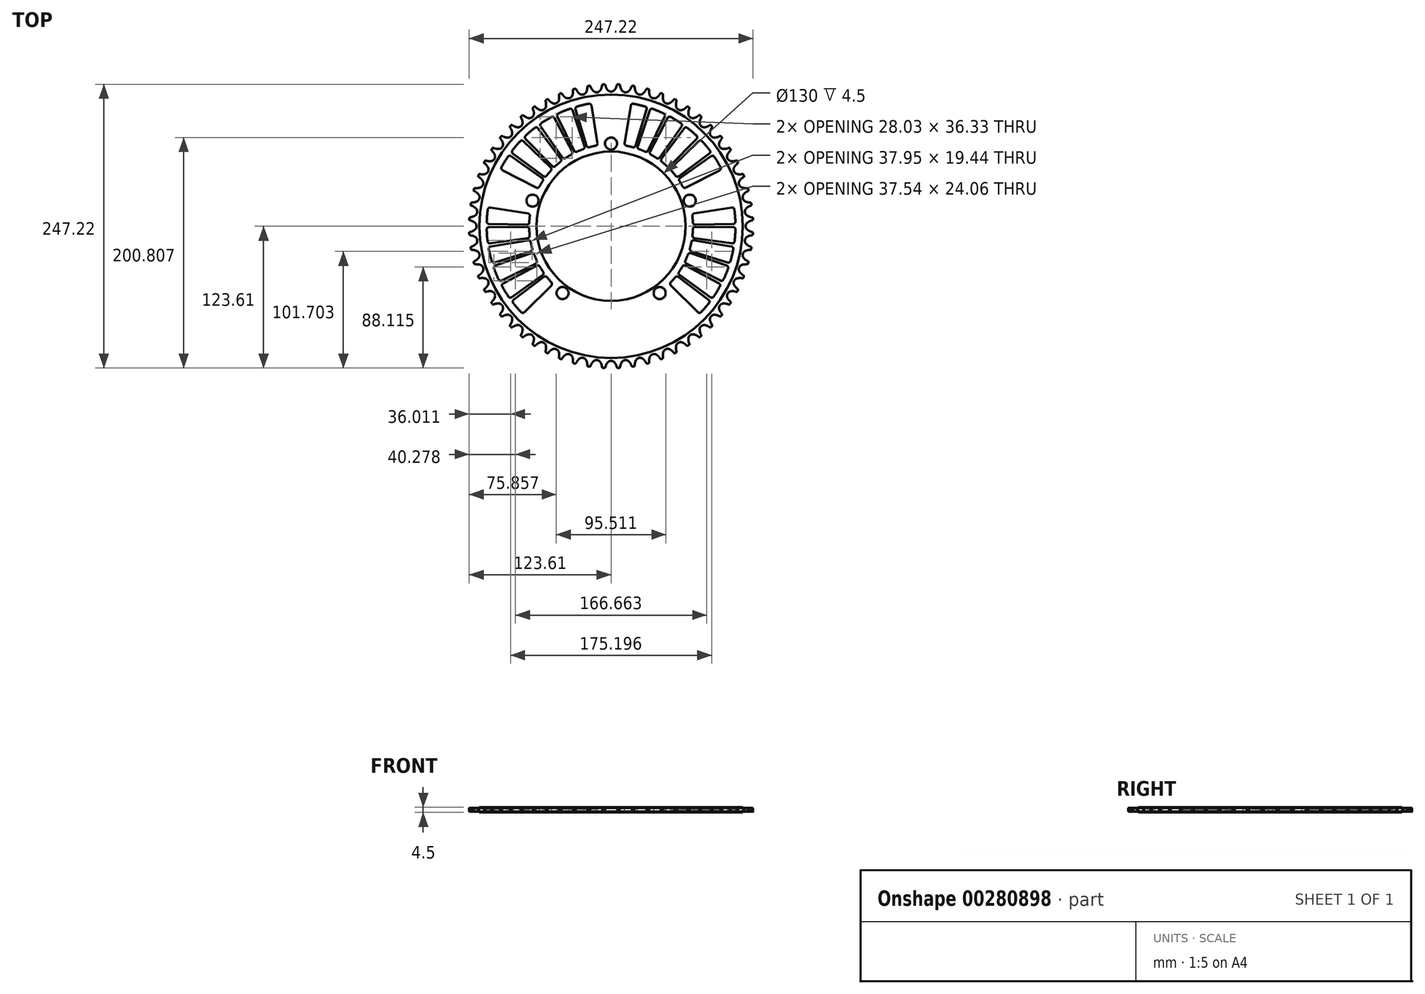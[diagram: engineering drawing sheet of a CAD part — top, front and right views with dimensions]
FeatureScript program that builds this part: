
annotation { "Feature Type Name" : "Feature", "Feature Type Description" : "" }
export const myFeature = defineFeature(function(context is Context, id is Id, definition is map)
    precondition{}
    {
        {
            var Q0;
            Q0=qCreatedBy(makeId("Top.planeOp"),FACE);
            var sketch = newSketch(context, id + "F0", { "sketchPlane" : qUnion([Q0])});
            skCircle(sketch, "E0", {"center": v(0, 0) * mm, "radius": 121.28 * mm, "construction": true});
            skArc(sketch, "E1", {"start": v(-3.25, 118.92) * mm, "mid": v(-1.82, 117.7) * mm, "end": v(0, 117.26) * mm});
            skArc(sketch, "E2", {"start": v(-4.69, 121.64) * mm, "mid": v(-4.07, 120.23) * mm, "end": v(-3.25, 118.92) * mm});
            skLineSegment(sketch, "E3", {"start": v(-4.69, 121.64) * mm, "end": v(-5.07, 122.77) * mm});
            skArc(sketch, "E4.trimOffspring", {"start": v(-5.07, 122.77) * mm, "mid": v(-5.68, 124.05) * mm, "end": v(-6.56, 125.17) * mm});
            skArc(sketch, "E5.MirrorCS", {"start": v(3.25, 118.92) * mm, "mid": v(1.82, 117.7) * mm, "end": v(0, 117.26) * mm});
            skArc(sketch, "E6.MirrorCS", {"start": v(4.69, 121.64) * mm, "mid": v(4.07, 120.23) * mm, "end": v(3.25, 118.92) * mm});
            skLineSegment(sketch, "E7.MirrorCS", {"start": v(4.69, 121.64) * mm, "end": v(5.07, 122.77) * mm});
            skArc(sketch, "E8.MirrorCS", {"start": v(5.07, 122.77) * mm, "mid": v(5.68, 124.05) * mm, "end": v(6.56, 125.17) * mm});
            skArc(sketch, "E9.1.1", {"start": v(-17.37, 120.49) * mm, "mid": v(-16.61, 119.14) * mm, "end": v(-15.66, 117.93) * mm});
            skArc(sketch, "E9.1.2", {"start": v(-8.06, 121.47) * mm, "mid": v(-8.52, 120) * mm, "end": v(-9.2, 118.6) * mm});
            skArc(sketch, "E9.1.3", {"start": v(-9.2, 118.6) * mm, "mid": v(-10.49, 117.24) * mm, "end": v(-12.26, 116.62) * mm});
            skArc(sketch, "E9.1.4", {"start": v(-7.79, 122.62) * mm, "mid": v(-7.32, 123.97) * mm, "end": v(-6.56, 125.17) * mm});
            skArc(sketch, "E9.1.5", {"start": v(-17.88, 121.56) * mm, "mid": v(-18.62, 122.78) * mm, "end": v(-19.6, 123.8) * mm});
            skArc(sketch, "E9.1.6", {"start": v(-15.66, 117.93) * mm, "mid": v(-14.12, 116.86) * mm, "end": v(-12.26, 116.62) * mm});
            skLineSegment(sketch, "E9.1.7", {"start": v(-17.37, 120.49) * mm, "end": v(-17.88, 121.56) * mm});
            skLineSegment(sketch, "E9.1.8", {"start": v(-8.06, 121.47) * mm, "end": v(-7.79, 122.62) * mm});
            skArc(sketch, "E9.2.1", {"start": v(-29.87, 118) * mm, "mid": v(-28.98, 116.75) * mm, "end": v(-27.9, 115.64) * mm});
            skArc(sketch, "E9.2.2", {"start": v(-20.7, 119.96) * mm, "mid": v(-21.02, 118.44) * mm, "end": v(-21.55, 117) * mm});
            skArc(sketch, "E9.2.3", {"start": v(-21.55, 117) * mm, "mid": v(-22.69, 115.5) * mm, "end": v(-24.38, 114.7) * mm});
            skArc(sketch, "E9.2.4", {"start": v(-20.56, 121.14) * mm, "mid": v(-20.24, 122.52) * mm, "end": v(-19.6, 123.8) * mm});
            skArc(sketch, "E9.2.5", {"start": v(-30.49, 119.03) * mm, "mid": v(-31.35, 120.16) * mm, "end": v(-32.44, 121.08) * mm});
            skArc(sketch, "E9.2.6", {"start": v(-27.9, 115.64) * mm, "mid": v(-26.25, 114.75) * mm, "end": v(-24.38, 114.7) * mm});
            skLineSegment(sketch, "E9.2.7", {"start": v(-29.87, 118) * mm, "end": v(-30.49, 119.03) * mm});
            skLineSegment(sketch, "E9.2.8", {"start": v(-20.7, 119.96) * mm, "end": v(-20.56, 121.14) * mm});
            skArc(sketch, "E9.3.1", {"start": v(-42.05, 114.24) * mm, "mid": v(-41.02, 113.08) * mm, "end": v(-39.84, 112.1) * mm});
            skArc(sketch, "E9.3.2", {"start": v(-33.13, 117.14) * mm, "mid": v(-33.28, 115.6) * mm, "end": v(-33.66, 114.1) * mm});
            skArc(sketch, "E9.3.3", {"start": v(-33.66, 114.1) * mm, "mid": v(-34.64, 112.5) * mm, "end": v(-36.24, 111.52) * mm});
            skArc(sketch, "E9.3.4", {"start": v(-33.11, 118.33) * mm, "mid": v(-32.93, 119.74) * mm, "end": v(-32.44, 121.08) * mm});
            skArc(sketch, "E9.3.5", {"start": v(-42.76, 115.2) * mm, "mid": v(-43.74, 116.23) * mm, "end": v(-44.92, 117.02) * mm});
            skArc(sketch, "E9.3.6", {"start": v(-39.84, 112.1) * mm, "mid": v(-38.1, 111.37) * mm, "end": v(-36.24, 111.52) * mm});
            skLineSegment(sketch, "E9.3.7", {"start": v(-42.05, 114.24) * mm, "end": v(-42.76, 115.2) * mm});
            skLineSegment(sketch, "E9.3.8", {"start": v(-33.13, 117.14) * mm, "end": v(-33.11, 118.33) * mm});
            skArc(sketch, "E9.4.1", {"start": v(-53.76, 109.22) * mm, "mid": v(-52.62, 108.18) * mm, "end": v(-51.34, 107.31) * mm});
            skArc(sketch, "E9.4.2", {"start": v(-45.2, 113.03) * mm, "mid": v(-45.18, 111.49) * mm, "end": v(-45.4, 109.96) * mm});
            skArc(sketch, "E9.4.3", {"start": v(-45.4, 109.96) * mm, "mid": v(-46.2, 108.26) * mm, "end": v(-47.7, 107.12) * mm});
            skArc(sketch, "E9.4.4", {"start": v(-45.3, 114.22) * mm, "mid": v(-45.27, 115.64) * mm, "end": v(-44.92, 117.02) * mm});
            skArc(sketch, "E9.4.5", {"start": v(-54.57, 110.1) * mm, "mid": v(-55.65, 111.02) * mm, "end": v(-56.9, 111.68) * mm});
            skArc(sketch, "E9.4.6", {"start": v(-51.34, 107.31) * mm, "mid": v(-49.54, 106.78) * mm, "end": v(-47.7, 107.12) * mm});
            skLineSegment(sketch, "E9.4.7", {"start": v(-53.76, 109.22) * mm, "end": v(-54.57, 110.1) * mm});
            skLineSegment(sketch, "E9.4.8", {"start": v(-45.2, 113.03) * mm, "end": v(-45.3, 114.22) * mm});
            skArc(sketch, "E9.5.1", {"start": v(-64.88, 103) * mm, "mid": v(-63.64, 102.08) * mm, "end": v(-62.27, 101.36) * mm});
            skArc(sketch, "E9.5.2", {"start": v(-56.76, 107.69) * mm, "mid": v(-56.59, 106.15) * mm, "end": v(-56.64, 104.6) * mm});
            skArc(sketch, "E9.5.3", {"start": v(-56.64, 104.6) * mm, "mid": v(-57.27, 102.84) * mm, "end": v(-58.63, 101.55) * mm});
            skArc(sketch, "E9.5.4", {"start": v(-57, 108.85) * mm, "mid": v(-57.1, 110.27) * mm, "end": v(-56.9, 111.68) * mm});
            skArc(sketch, "E9.5.5", {"start": v(-65.78, 103.78) * mm, "mid": v(-66.95, 104.6) * mm, "end": v(-68.27, 105.12) * mm});
            skArc(sketch, "E9.5.6", {"start": v(-62.27, 101.36) * mm, "mid": v(-60.43, 101.02) * mm, "end": v(-58.63, 101.55) * mm});
            skLineSegment(sketch, "E9.5.7", {"start": v(-64.88, 103) * mm, "end": v(-65.78, 103.78) * mm});
            skLineSegment(sketch, "E9.5.8", {"start": v(-56.76, 107.69) * mm, "end": v(-57, 108.85) * mm});
            skArc(sketch, "E9.6.1", {"start": v(-75.3, 95.66) * mm, "mid": v(-73.96, 94.87) * mm, "end": v(-72.53, 94.3) * mm});
            skArc(sketch, "E9.6.2", {"start": v(-67.7, 101.16) * mm, "mid": v(-67.38, 99.66) * mm, "end": v(-67.27, 98.11) * mm});
            skArc(sketch, "E9.6.3", {"start": v(-67.27, 98.11) * mm, "mid": v(-67.7, 96.3) * mm, "end": v(-68.92, 94.87) * mm});
            skArc(sketch, "E9.6.4", {"start": v(-68.06, 102.3) * mm, "mid": v(-68.32, 103.7) * mm, "end": v(-68.27, 105.12) * mm});
            skArc(sketch, "E9.6.5", {"start": v(-76.26, 96.34) * mm, "mid": v(-77.51, 97.02) * mm, "end": v(-78.88, 97.41) * mm});
            skArc(sketch, "E9.6.6", {"start": v(-72.53, 94.3) * mm, "mid": v(-70.66, 94.15) * mm, "end": v(-68.92, 94.87) * mm});
            skLineSegment(sketch, "E9.6.7", {"start": v(-75.3, 95.66) * mm, "end": v(-76.26, 96.34) * mm});
            skLineSegment(sketch, "E9.6.8", {"start": v(-67.7, 101.16) * mm, "end": v(-68.06, 102.3) * mm});
            skArc(sketch, "E9.7.1", {"start": v(-84.88, 87.26) * mm, "mid": v(-83.47, 86.62) * mm, "end": v(-81.98, 86.2) * mm});
            skArc(sketch, "E9.7.2", {"start": v(-77.91, 93.53) * mm, "mid": v(-77.42, 92.07) * mm, "end": v(-77.16, 90.55) * mm});
            skArc(sketch, "E9.7.3", {"start": v(-77.16, 90.55) * mm, "mid": v(-77.4, 88.69) * mm, "end": v(-78.46, 87.14) * mm});
            skArc(sketch, "E9.7.4", {"start": v(-78.38, 94.63) * mm, "mid": v(-78.79, 96) * mm, "end": v(-78.88, 97.41) * mm});
            skArc(sketch, "E9.7.5", {"start": v(-85.92, 87.84) * mm, "mid": v(-87.23, 88.39) * mm, "end": v(-88.63, 88.63) * mm});
            skArc(sketch, "E9.7.6", {"start": v(-81.98, 86.2) * mm, "mid": v(-80.11, 86.25) * mm, "end": v(-78.46, 87.14) * mm});
            skLineSegment(sketch, "E9.7.7", {"start": v(-84.88, 87.26) * mm, "end": v(-85.92, 87.84) * mm});
            skLineSegment(sketch, "E9.7.8", {"start": v(-77.91, 93.53) * mm, "end": v(-78.38, 94.63) * mm});
            skArc(sketch, "E9.8.1", {"start": v(-93.53, 77.91) * mm, "mid": v(-92.07, 77.42) * mm, "end": v(-90.55, 77.16) * mm});
            skArc(sketch, "E9.8.2", {"start": v(-87.26, 84.88) * mm, "mid": v(-86.62, 83.47) * mm, "end": v(-86.2, 81.98) * mm});
            skArc(sketch, "E9.8.3", {"start": v(-86.2, 81.98) * mm, "mid": v(-86.25, 80.11) * mm, "end": v(-87.14, 78.46) * mm});
            skArc(sketch, "E9.8.4", {"start": v(-87.84, 85.92) * mm, "mid": v(-88.39, 87.23) * mm, "end": v(-88.63, 88.63) * mm});
            skArc(sketch, "E9.8.5", {"start": v(-94.63, 78.38) * mm, "mid": v(-96, 78.79) * mm, "end": v(-97.41, 78.88) * mm});
            skArc(sketch, "E9.8.6", {"start": v(-90.55, 77.16) * mm, "mid": v(-88.69, 77.4) * mm, "end": v(-87.14, 78.46) * mm});
            skLineSegment(sketch, "E9.8.7", {"start": v(-93.53, 77.91) * mm, "end": v(-94.63, 78.38) * mm});
            skLineSegment(sketch, "E9.8.8", {"start": v(-87.26, 84.88) * mm, "end": v(-87.84, 85.92) * mm});
            skArc(sketch, "E9.9.1", {"start": v(-101.16, 67.7) * mm, "mid": v(-99.66, 67.38) * mm, "end": v(-98.11, 67.27) * mm});
            skArc(sketch, "E9.9.2", {"start": v(-95.66, 75.3) * mm, "mid": v(-94.87, 73.96) * mm, "end": v(-94.3, 72.53) * mm});
            skArc(sketch, "E9.9.3", {"start": v(-94.3, 72.53) * mm, "mid": v(-94.15, 70.66) * mm, "end": v(-94.87, 68.92) * mm});
            skArc(sketch, "E9.9.4", {"start": v(-96.34, 76.26) * mm, "mid": v(-97.02, 77.51) * mm, "end": v(-97.41, 78.88) * mm});
            skArc(sketch, "E9.9.5", {"start": v(-102.3, 68.06) * mm, "mid": v(-103.7, 68.32) * mm, "end": v(-105.12, 68.27) * mm});
            skArc(sketch, "E9.9.6", {"start": v(-98.11, 67.27) * mm, "mid": v(-96.3, 67.7) * mm, "end": v(-94.87, 68.92) * mm});
            skLineSegment(sketch, "E9.9.7", {"start": v(-101.16, 67.7) * mm, "end": v(-102.3, 68.06) * mm});
            skLineSegment(sketch, "E9.9.8", {"start": v(-95.66, 75.3) * mm, "end": v(-96.34, 76.26) * mm});
            skArc(sketch, "E9.10.1", {"start": v(-107.69, 56.76) * mm, "mid": v(-106.15, 56.59) * mm, "end": v(-104.6, 56.64) * mm});
            skArc(sketch, "E9.10.2", {"start": v(-103, 64.88) * mm, "mid": v(-102.08, 63.64) * mm, "end": v(-101.36, 62.27) * mm});
            skArc(sketch, "E9.10.3", {"start": v(-101.36, 62.27) * mm, "mid": v(-101.02, 60.43) * mm, "end": v(-101.55, 58.63) * mm});
            skArc(sketch, "E9.10.4", {"start": v(-103.78, 65.78) * mm, "mid": v(-104.6, 66.95) * mm, "end": v(-105.12, 68.27) * mm});
            skArc(sketch, "E9.10.5", {"start": v(-108.85, 57) * mm, "mid": v(-110.27, 57.1) * mm, "end": v(-111.68, 56.9) * mm});
            skArc(sketch, "E9.10.6", {"start": v(-104.6, 56.64) * mm, "mid": v(-102.84, 57.27) * mm, "end": v(-101.55, 58.63) * mm});
            skLineSegment(sketch, "E9.10.7", {"start": v(-107.69, 56.76) * mm, "end": v(-108.85, 57) * mm});
            skLineSegment(sketch, "E9.10.8", {"start": v(-103, 64.88) * mm, "end": v(-103.78, 65.78) * mm});
            skArc(sketch, "E9.11.1", {"start": v(-113.03, 45.2) * mm, "mid": v(-111.49, 45.18) * mm, "end": v(-109.96, 45.4) * mm});
            skArc(sketch, "E9.11.2", {"start": v(-109.22, 53.76) * mm, "mid": v(-108.18, 52.62) * mm, "end": v(-107.31, 51.34) * mm});
            skArc(sketch, "E9.11.3", {"start": v(-107.31, 51.34) * mm, "mid": v(-106.78, 49.54) * mm, "end": v(-107.12, 47.7) * mm});
            skArc(sketch, "E9.11.4", {"start": v(-110.1, 54.57) * mm, "mid": v(-111.02, 55.65) * mm, "end": v(-111.68, 56.9) * mm});
            skArc(sketch, "E9.11.5", {"start": v(-114.22, 45.3) * mm, "mid": v(-115.64, 45.27) * mm, "end": v(-117.02, 44.92) * mm});
            skArc(sketch, "E9.11.6", {"start": v(-109.96, 45.4) * mm, "mid": v(-108.26, 46.2) * mm, "end": v(-107.12, 47.7) * mm});
            skLineSegment(sketch, "E9.11.7", {"start": v(-113.03, 45.2) * mm, "end": v(-114.22, 45.3) * mm});
            skLineSegment(sketch, "E9.11.8", {"start": v(-109.22, 53.76) * mm, "end": v(-110.1, 54.57) * mm});
            skArc(sketch, "E9.12.1", {"start": v(-117.14, 33.13) * mm, "mid": v(-115.6, 33.28) * mm, "end": v(-114.1, 33.66) * mm});
            skArc(sketch, "E9.12.2", {"start": v(-114.24, 42.05) * mm, "mid": v(-113.08, 41.02) * mm, "end": v(-112.1, 39.84) * mm});
            skArc(sketch, "E9.12.3", {"start": v(-112.1, 39.84) * mm, "mid": v(-111.37, 38.1) * mm, "end": v(-111.52, 36.24) * mm});
            skArc(sketch, "E9.12.4", {"start": v(-115.2, 42.76) * mm, "mid": v(-116.23, 43.74) * mm, "end": v(-117.02, 44.92) * mm});
            skArc(sketch, "E9.12.5", {"start": v(-118.33, 33.11) * mm, "mid": v(-119.74, 32.93) * mm, "end": v(-121.08, 32.44) * mm});
            skArc(sketch, "E9.12.6", {"start": v(-114.1, 33.66) * mm, "mid": v(-112.5, 34.64) * mm, "end": v(-111.52, 36.24) * mm});
            skLineSegment(sketch, "E9.12.7", {"start": v(-117.14, 33.13) * mm, "end": v(-118.33, 33.11) * mm});
            skLineSegment(sketch, "E9.12.8", {"start": v(-114.24, 42.05) * mm, "end": v(-115.2, 42.76) * mm});
            skArc(sketch, "E9.13.1", {"start": v(-119.96, 20.7) * mm, "mid": v(-118.44, 21.02) * mm, "end": v(-117, 21.55) * mm});
            skArc(sketch, "E9.13.2", {"start": v(-118, 29.87) * mm, "mid": v(-116.75, 28.98) * mm, "end": v(-115.64, 27.9) * mm});
            skArc(sketch, "E9.13.3", {"start": v(-115.64, 27.9) * mm, "mid": v(-114.75, 26.25) * mm, "end": v(-114.7, 24.38) * mm});
            skArc(sketch, "E9.13.4", {"start": v(-119.03, 30.49) * mm, "mid": v(-120.16, 31.35) * mm, "end": v(-121.08, 32.44) * mm});
            skArc(sketch, "E9.13.5", {"start": v(-121.14, 20.56) * mm, "mid": v(-122.52, 20.24) * mm, "end": v(-123.8, 19.6) * mm});
            skArc(sketch, "E9.13.6", {"start": v(-117, 21.55) * mm, "mid": v(-115.5, 22.69) * mm, "end": v(-114.7, 24.38) * mm});
            skLineSegment(sketch, "E9.13.7", {"start": v(-119.96, 20.7) * mm, "end": v(-121.14, 20.56) * mm});
            skLineSegment(sketch, "E9.13.8", {"start": v(-118, 29.87) * mm, "end": v(-119.03, 30.49) * mm});
            skArc(sketch, "E9.14.1", {"start": v(-121.47, 8.06) * mm, "mid": v(-120, 8.52) * mm, "end": v(-118.6, 9.2) * mm});
            skArc(sketch, "E9.14.2", {"start": v(-120.49, 17.37) * mm, "mid": v(-119.14, 16.61) * mm, "end": v(-117.93, 15.66) * mm});
            skArc(sketch, "E9.14.3", {"start": v(-117.93, 15.66) * mm, "mid": v(-116.86, 14.12) * mm, "end": v(-116.62, 12.26) * mm});
            skArc(sketch, "E9.14.4", {"start": v(-121.56, 17.88) * mm, "mid": v(-122.78, 18.62) * mm, "end": v(-123.8, 19.6) * mm});
            skArc(sketch, "E9.14.5", {"start": v(-122.62, 7.79) * mm, "mid": v(-123.97, 7.32) * mm, "end": v(-125.17, 6.56) * mm});
            skArc(sketch, "E9.14.6", {"start": v(-118.6, 9.2) * mm, "mid": v(-117.24, 10.49) * mm, "end": v(-116.62, 12.26) * mm});
            skLineSegment(sketch, "E9.14.7", {"start": v(-121.47, 8.06) * mm, "end": v(-122.62, 7.79) * mm});
            skLineSegment(sketch, "E9.14.8", {"start": v(-120.49, 17.37) * mm, "end": v(-121.56, 17.88) * mm});
            skArc(sketch, "E9.15.1", {"start": v(-121.64, -4.69) * mm, "mid": v(-120.23, -4.07) * mm, "end": v(-118.92, -3.25) * mm});
            skArc(sketch, "E9.15.2", {"start": v(-121.64, 4.69) * mm, "mid": v(-120.23, 4.07) * mm, "end": v(-118.92, 3.25) * mm});
            skArc(sketch, "E9.15.3", {"start": v(-118.92, 3.25) * mm, "mid": v(-117.7, 1.82) * mm, "end": v(-117.26, 0) * mm});
            skArc(sketch, "E9.15.4", {"start": v(-122.77, 5.07) * mm, "mid": v(-124.05, 5.68) * mm, "end": v(-125.17, 6.56) * mm});
            skArc(sketch, "E9.15.5", {"start": v(-122.77, -5.07) * mm, "mid": v(-124.05, -5.68) * mm, "end": v(-125.17, -6.56) * mm});
            skArc(sketch, "E9.15.6", {"start": v(-118.92, -3.25) * mm, "mid": v(-117.7, -1.82) * mm, "end": v(-117.26, 0) * mm});
            skLineSegment(sketch, "E9.15.7", {"start": v(-121.64, -4.69) * mm, "end": v(-122.77, -5.07) * mm});
            skLineSegment(sketch, "E9.15.8", {"start": v(-121.64, 4.69) * mm, "end": v(-122.77, 5.07) * mm});
            skArc(sketch, "E9.16.1", {"start": v(-120.49, -17.37) * mm, "mid": v(-119.14, -16.61) * mm, "end": v(-117.93, -15.66) * mm});
            skArc(sketch, "E9.16.2", {"start": v(-121.47, -8.06) * mm, "mid": v(-120, -8.52) * mm, "end": v(-118.6, -9.2) * mm});
            skArc(sketch, "E9.16.3", {"start": v(-118.6, -9.2) * mm, "mid": v(-117.24, -10.49) * mm, "end": v(-116.62, -12.26) * mm});
            skArc(sketch, "E9.16.4", {"start": v(-122.62, -7.79) * mm, "mid": v(-123.97, -7.32) * mm, "end": v(-125.17, -6.56) * mm});
            skArc(sketch, "E9.16.5", {"start": v(-121.56, -17.88) * mm, "mid": v(-122.78, -18.62) * mm, "end": v(-123.8, -19.6) * mm});
            skArc(sketch, "E9.16.6", {"start": v(-117.93, -15.66) * mm, "mid": v(-116.86, -14.12) * mm, "end": v(-116.62, -12.26) * mm});
            skLineSegment(sketch, "E9.16.7", {"start": v(-120.49, -17.37) * mm, "end": v(-121.56, -17.88) * mm});
            skLineSegment(sketch, "E9.16.8", {"start": v(-121.47, -8.06) * mm, "end": v(-122.62, -7.79) * mm});
            skArc(sketch, "E9.17.1", {"start": v(-118, -29.87) * mm, "mid": v(-116.75, -28.98) * mm, "end": v(-115.64, -27.9) * mm});
            skArc(sketch, "E9.17.2", {"start": v(-119.96, -20.7) * mm, "mid": v(-118.44, -21.02) * mm, "end": v(-117, -21.55) * mm});
            skArc(sketch, "E9.17.3", {"start": v(-117, -21.55) * mm, "mid": v(-115.5, -22.69) * mm, "end": v(-114.7, -24.38) * mm});
            skArc(sketch, "E9.17.4", {"start": v(-121.14, -20.56) * mm, "mid": v(-122.52, -20.24) * mm, "end": v(-123.8, -19.6) * mm});
            skArc(sketch, "E9.17.5", {"start": v(-119.03, -30.49) * mm, "mid": v(-120.16, -31.35) * mm, "end": v(-121.08, -32.44) * mm});
            skArc(sketch, "E9.17.6", {"start": v(-115.64, -27.9) * mm, "mid": v(-114.75, -26.25) * mm, "end": v(-114.7, -24.38) * mm});
            skLineSegment(sketch, "E9.17.7", {"start": v(-118, -29.87) * mm, "end": v(-119.03, -30.49) * mm});
            skLineSegment(sketch, "E9.17.8", {"start": v(-119.96, -20.7) * mm, "end": v(-121.14, -20.56) * mm});
            skArc(sketch, "E9.18.1", {"start": v(-114.24, -42.05) * mm, "mid": v(-113.08, -41.02) * mm, "end": v(-112.1, -39.84) * mm});
            skArc(sketch, "E9.18.2", {"start": v(-117.14, -33.13) * mm, "mid": v(-115.6, -33.28) * mm, "end": v(-114.1, -33.66) * mm});
            skArc(sketch, "E9.18.3", {"start": v(-114.1, -33.66) * mm, "mid": v(-112.5, -34.64) * mm, "end": v(-111.52, -36.24) * mm});
            skArc(sketch, "E9.18.4", {"start": v(-118.33, -33.11) * mm, "mid": v(-119.74, -32.93) * mm, "end": v(-121.08, -32.44) * mm});
            skArc(sketch, "E9.18.5", {"start": v(-115.2, -42.76) * mm, "mid": v(-116.23, -43.74) * mm, "end": v(-117.02, -44.92) * mm});
            skArc(sketch, "E9.18.6", {"start": v(-112.1, -39.84) * mm, "mid": v(-111.37, -38.1) * mm, "end": v(-111.52, -36.24) * mm});
            skLineSegment(sketch, "E9.18.7", {"start": v(-114.24, -42.05) * mm, "end": v(-115.2, -42.76) * mm});
            skLineSegment(sketch, "E9.18.8", {"start": v(-117.14, -33.13) * mm, "end": v(-118.33, -33.11) * mm});
            skArc(sketch, "E9.19.1", {"start": v(-109.22, -53.76) * mm, "mid": v(-108.18, -52.62) * mm, "end": v(-107.31, -51.34) * mm});
            skArc(sketch, "E9.19.2", {"start": v(-113.03, -45.2) * mm, "mid": v(-111.49, -45.18) * mm, "end": v(-109.96, -45.4) * mm});
            skArc(sketch, "E9.19.3", {"start": v(-109.96, -45.4) * mm, "mid": v(-108.26, -46.2) * mm, "end": v(-107.12, -47.7) * mm});
            skArc(sketch, "E9.19.4", {"start": v(-114.22, -45.3) * mm, "mid": v(-115.64, -45.27) * mm, "end": v(-117.02, -44.92) * mm});
            skArc(sketch, "E9.19.5", {"start": v(-110.1, -54.57) * mm, "mid": v(-111.02, -55.65) * mm, "end": v(-111.68, -56.9) * mm});
            skArc(sketch, "E9.19.6", {"start": v(-107.31, -51.34) * mm, "mid": v(-106.78, -49.54) * mm, "end": v(-107.12, -47.7) * mm});
            skLineSegment(sketch, "E9.19.7", {"start": v(-109.22, -53.76) * mm, "end": v(-110.1, -54.57) * mm});
            skLineSegment(sketch, "E9.19.8", {"start": v(-113.03, -45.2) * mm, "end": v(-114.22, -45.3) * mm});
            skArc(sketch, "E9.20.1", {"start": v(-103, -64.88) * mm, "mid": v(-102.08, -63.64) * mm, "end": v(-101.36, -62.27) * mm});
            skArc(sketch, "E9.20.2", {"start": v(-107.69, -56.76) * mm, "mid": v(-106.15, -56.59) * mm, "end": v(-104.6, -56.64) * mm});
            skArc(sketch, "E9.20.3", {"start": v(-104.6, -56.64) * mm, "mid": v(-102.84, -57.27) * mm, "end": v(-101.55, -58.63) * mm});
            skArc(sketch, "E9.20.4", {"start": v(-108.85, -57) * mm, "mid": v(-110.27, -57.1) * mm, "end": v(-111.68, -56.9) * mm});
            skArc(sketch, "E9.20.5", {"start": v(-103.78, -65.78) * mm, "mid": v(-104.6, -66.95) * mm, "end": v(-105.12, -68.27) * mm});
            skArc(sketch, "E9.20.6", {"start": v(-101.36, -62.27) * mm, "mid": v(-101.02, -60.43) * mm, "end": v(-101.55, -58.63) * mm});
            skLineSegment(sketch, "E9.20.7", {"start": v(-103, -64.88) * mm, "end": v(-103.78, -65.78) * mm});
            skLineSegment(sketch, "E9.20.8", {"start": v(-107.69, -56.76) * mm, "end": v(-108.85, -57) * mm});
            skArc(sketch, "E9.21.1", {"start": v(-95.66, -75.3) * mm, "mid": v(-94.87, -73.96) * mm, "end": v(-94.3, -72.53) * mm});
            skArc(sketch, "E9.21.2", {"start": v(-101.16, -67.7) * mm, "mid": v(-99.66, -67.38) * mm, "end": v(-98.11, -67.27) * mm});
            skArc(sketch, "E9.21.3", {"start": v(-98.11, -67.27) * mm, "mid": v(-96.3, -67.7) * mm, "end": v(-94.87, -68.92) * mm});
            skArc(sketch, "E9.21.4", {"start": v(-102.3, -68.06) * mm, "mid": v(-103.7, -68.32) * mm, "end": v(-105.12, -68.27) * mm});
            skArc(sketch, "E9.21.5", {"start": v(-96.34, -76.26) * mm, "mid": v(-97.02, -77.51) * mm, "end": v(-97.41, -78.88) * mm});
            skArc(sketch, "E9.21.6", {"start": v(-94.3, -72.53) * mm, "mid": v(-94.15, -70.66) * mm, "end": v(-94.87, -68.92) * mm});
            skLineSegment(sketch, "E9.21.7", {"start": v(-95.66, -75.3) * mm, "end": v(-96.34, -76.26) * mm});
            skLineSegment(sketch, "E9.21.8", {"start": v(-101.16, -67.7) * mm, "end": v(-102.3, -68.06) * mm});
            skArc(sketch, "E9.22.1", {"start": v(-87.26, -84.88) * mm, "mid": v(-86.62, -83.47) * mm, "end": v(-86.2, -81.98) * mm});
            skArc(sketch, "E9.22.2", {"start": v(-93.53, -77.91) * mm, "mid": v(-92.07, -77.42) * mm, "end": v(-90.55, -77.16) * mm});
            skArc(sketch, "E9.22.3", {"start": v(-90.55, -77.16) * mm, "mid": v(-88.69, -77.4) * mm, "end": v(-87.14, -78.46) * mm});
            skArc(sketch, "E9.22.4", {"start": v(-94.63, -78.38) * mm, "mid": v(-96, -78.79) * mm, "end": v(-97.41, -78.88) * mm});
            skArc(sketch, "E9.22.5", {"start": v(-87.84, -85.92) * mm, "mid": v(-88.39, -87.23) * mm, "end": v(-88.63, -88.63) * mm});
            skArc(sketch, "E9.22.6", {"start": v(-86.2, -81.98) * mm, "mid": v(-86.25, -80.11) * mm, "end": v(-87.14, -78.46) * mm});
            skLineSegment(sketch, "E9.22.7", {"start": v(-87.26, -84.88) * mm, "end": v(-87.84, -85.92) * mm});
            skLineSegment(sketch, "E9.22.8", {"start": v(-93.53, -77.91) * mm, "end": v(-94.63, -78.38) * mm});
            skArc(sketch, "E9.23.1", {"start": v(-77.91, -93.53) * mm, "mid": v(-77.42, -92.07) * mm, "end": v(-77.16, -90.55) * mm});
            skArc(sketch, "E9.23.2", {"start": v(-84.88, -87.26) * mm, "mid": v(-83.47, -86.62) * mm, "end": v(-81.98, -86.2) * mm});
            skArc(sketch, "E9.23.3", {"start": v(-81.98, -86.2) * mm, "mid": v(-80.11, -86.25) * mm, "end": v(-78.46, -87.14) * mm});
            skArc(sketch, "E9.23.4", {"start": v(-85.92, -87.84) * mm, "mid": v(-87.23, -88.39) * mm, "end": v(-88.63, -88.63) * mm});
            skArc(sketch, "E9.23.5", {"start": v(-78.38, -94.63) * mm, "mid": v(-78.79, -96) * mm, "end": v(-78.88, -97.41) * mm});
            skArc(sketch, "E9.23.6", {"start": v(-77.16, -90.55) * mm, "mid": v(-77.4, -88.69) * mm, "end": v(-78.46, -87.14) * mm});
            skLineSegment(sketch, "E9.23.7", {"start": v(-77.91, -93.53) * mm, "end": v(-78.38, -94.63) * mm});
            skLineSegment(sketch, "E9.23.8", {"start": v(-84.88, -87.26) * mm, "end": v(-85.92, -87.84) * mm});
            skArc(sketch, "E9.24.1", {"start": v(-67.7, -101.16) * mm, "mid": v(-67.38, -99.66) * mm, "end": v(-67.27, -98.11) * mm});
            skArc(sketch, "E9.24.2", {"start": v(-75.3, -95.66) * mm, "mid": v(-73.96, -94.87) * mm, "end": v(-72.53, -94.3) * mm});
            skArc(sketch, "E9.24.3", {"start": v(-72.53, -94.3) * mm, "mid": v(-70.66, -94.15) * mm, "end": v(-68.92, -94.87) * mm});
            skArc(sketch, "E9.24.4", {"start": v(-76.26, -96.34) * mm, "mid": v(-77.51, -97.02) * mm, "end": v(-78.88, -97.41) * mm});
            skArc(sketch, "E9.24.5", {"start": v(-68.06, -102.3) * mm, "mid": v(-68.32, -103.7) * mm, "end": v(-68.27, -105.12) * mm});
            skArc(sketch, "E9.24.6", {"start": v(-67.27, -98.11) * mm, "mid": v(-67.7, -96.3) * mm, "end": v(-68.92, -94.87) * mm});
            skLineSegment(sketch, "E9.24.7", {"start": v(-67.7, -101.16) * mm, "end": v(-68.06, -102.3) * mm});
            skLineSegment(sketch, "E9.24.8", {"start": v(-75.3, -95.66) * mm, "end": v(-76.26, -96.34) * mm});
            skArc(sketch, "E9.25.1", {"start": v(-56.76, -107.69) * mm, "mid": v(-56.59, -106.15) * mm, "end": v(-56.64, -104.6) * mm});
            skArc(sketch, "E9.25.2", {"start": v(-64.88, -103) * mm, "mid": v(-63.64, -102.08) * mm, "end": v(-62.27, -101.36) * mm});
            skArc(sketch, "E9.25.3", {"start": v(-62.27, -101.36) * mm, "mid": v(-60.43, -101.02) * mm, "end": v(-58.63, -101.55) * mm});
            skArc(sketch, "E9.25.4", {"start": v(-65.78, -103.78) * mm, "mid": v(-66.95, -104.6) * mm, "end": v(-68.27, -105.12) * mm});
            skArc(sketch, "E9.25.5", {"start": v(-57, -108.85) * mm, "mid": v(-57.1, -110.27) * mm, "end": v(-56.9, -111.68) * mm});
            skArc(sketch, "E9.25.6", {"start": v(-56.64, -104.6) * mm, "mid": v(-57.27, -102.84) * mm, "end": v(-58.63, -101.55) * mm});
            skLineSegment(sketch, "E9.25.7", {"start": v(-56.76, -107.69) * mm, "end": v(-57, -108.85) * mm});
            skLineSegment(sketch, "E9.25.8", {"start": v(-64.88, -103) * mm, "end": v(-65.78, -103.78) * mm});
            skArc(sketch, "E9.26.1", {"start": v(-45.2, -113.03) * mm, "mid": v(-45.18, -111.49) * mm, "end": v(-45.4, -109.96) * mm});
            skArc(sketch, "E9.26.2", {"start": v(-53.76, -109.22) * mm, "mid": v(-52.62, -108.18) * mm, "end": v(-51.34, -107.31) * mm});
            skArc(sketch, "E9.26.3", {"start": v(-51.34, -107.31) * mm, "mid": v(-49.54, -106.78) * mm, "end": v(-47.7, -107.12) * mm});
            skArc(sketch, "E9.26.4", {"start": v(-54.57, -110.1) * mm, "mid": v(-55.65, -111.02) * mm, "end": v(-56.9, -111.68) * mm});
            skArc(sketch, "E9.26.5", {"start": v(-45.3, -114.22) * mm, "mid": v(-45.27, -115.64) * mm, "end": v(-44.92, -117.02) * mm});
            skArc(sketch, "E9.26.6", {"start": v(-45.4, -109.96) * mm, "mid": v(-46.2, -108.26) * mm, "end": v(-47.7, -107.12) * mm});
            skLineSegment(sketch, "E9.26.7", {"start": v(-45.2, -113.03) * mm, "end": v(-45.3, -114.22) * mm});
            skLineSegment(sketch, "E9.26.8", {"start": v(-53.76, -109.22) * mm, "end": v(-54.57, -110.1) * mm});
            skArc(sketch, "E9.27.1", {"start": v(-33.13, -117.14) * mm, "mid": v(-33.28, -115.6) * mm, "end": v(-33.66, -114.1) * mm});
            skArc(sketch, "E9.27.2", {"start": v(-42.05, -114.24) * mm, "mid": v(-41.02, -113.08) * mm, "end": v(-39.84, -112.1) * mm});
            skArc(sketch, "E9.27.3", {"start": v(-39.84, -112.1) * mm, "mid": v(-38.1, -111.37) * mm, "end": v(-36.24, -111.52) * mm});
            skArc(sketch, "E9.27.4", {"start": v(-42.76, -115.2) * mm, "mid": v(-43.74, -116.23) * mm, "end": v(-44.92, -117.02) * mm});
            skArc(sketch, "E9.27.5", {"start": v(-33.11, -118.33) * mm, "mid": v(-32.93, -119.74) * mm, "end": v(-32.44, -121.08) * mm});
            skArc(sketch, "E9.27.6", {"start": v(-33.66, -114.1) * mm, "mid": v(-34.64, -112.5) * mm, "end": v(-36.24, -111.52) * mm});
            skLineSegment(sketch, "E9.27.7", {"start": v(-33.13, -117.14) * mm, "end": v(-33.11, -118.33) * mm});
            skLineSegment(sketch, "E9.27.8", {"start": v(-42.05, -114.24) * mm, "end": v(-42.76, -115.2) * mm});
            skArc(sketch, "E9.28.1", {"start": v(-20.7, -119.96) * mm, "mid": v(-21.02, -118.44) * mm, "end": v(-21.55, -117) * mm});
            skArc(sketch, "E9.28.2", {"start": v(-29.87, -118) * mm, "mid": v(-28.98, -116.75) * mm, "end": v(-27.9, -115.64) * mm});
            skArc(sketch, "E9.28.3", {"start": v(-27.9, -115.64) * mm, "mid": v(-26.25, -114.75) * mm, "end": v(-24.38, -114.7) * mm});
            skArc(sketch, "E9.28.4", {"start": v(-30.49, -119.03) * mm, "mid": v(-31.35, -120.16) * mm, "end": v(-32.44, -121.08) * mm});
            skArc(sketch, "E9.28.5", {"start": v(-20.56, -121.14) * mm, "mid": v(-20.24, -122.52) * mm, "end": v(-19.6, -123.8) * mm});
            skArc(sketch, "E9.28.6", {"start": v(-21.55, -117) * mm, "mid": v(-22.69, -115.5) * mm, "end": v(-24.38, -114.7) * mm});
            skLineSegment(sketch, "E9.28.7", {"start": v(-20.7, -119.96) * mm, "end": v(-20.56, -121.14) * mm});
            skLineSegment(sketch, "E9.28.8", {"start": v(-29.87, -118) * mm, "end": v(-30.49, -119.03) * mm});
            skArc(sketch, "E9.29.1", {"start": v(-8.06, -121.47) * mm, "mid": v(-8.52, -120) * mm, "end": v(-9.2, -118.6) * mm});
            skArc(sketch, "E9.29.2", {"start": v(-17.37, -120.49) * mm, "mid": v(-16.61, -119.14) * mm, "end": v(-15.66, -117.93) * mm});
            skArc(sketch, "E9.29.3", {"start": v(-15.66, -117.93) * mm, "mid": v(-14.12, -116.86) * mm, "end": v(-12.26, -116.62) * mm});
            skArc(sketch, "E9.29.4", {"start": v(-17.88, -121.56) * mm, "mid": v(-18.62, -122.78) * mm, "end": v(-19.6, -123.8) * mm});
            skArc(sketch, "E9.29.5", {"start": v(-7.79, -122.62) * mm, "mid": v(-7.32, -123.97) * mm, "end": v(-6.56, -125.17) * mm});
            skArc(sketch, "E9.29.6", {"start": v(-9.2, -118.6) * mm, "mid": v(-10.49, -117.24) * mm, "end": v(-12.26, -116.62) * mm});
            skLineSegment(sketch, "E9.29.7", {"start": v(-8.06, -121.47) * mm, "end": v(-7.79, -122.62) * mm});
            skLineSegment(sketch, "E9.29.8", {"start": v(-17.37, -120.49) * mm, "end": v(-17.88, -121.56) * mm});
            skArc(sketch, "E9.30.1", {"start": v(4.69, -121.64) * mm, "mid": v(4.07, -120.23) * mm, "end": v(3.25, -118.92) * mm});
            skArc(sketch, "E9.30.2", {"start": v(-4.69, -121.64) * mm, "mid": v(-4.07, -120.23) * mm, "end": v(-3.25, -118.92) * mm});
            skArc(sketch, "E9.30.3", {"start": v(-3.25, -118.92) * mm, "mid": v(-1.82, -117.7) * mm, "end": v(0, -117.26) * mm});
            skArc(sketch, "E9.30.4", {"start": v(-5.07, -122.77) * mm, "mid": v(-5.68, -124.05) * mm, "end": v(-6.56, -125.17) * mm});
            skArc(sketch, "E9.30.5", {"start": v(5.07, -122.77) * mm, "mid": v(5.68, -124.05) * mm, "end": v(6.56, -125.17) * mm});
            skArc(sketch, "E9.30.6", {"start": v(3.25, -118.92) * mm, "mid": v(1.82, -117.7) * mm, "end": v(0, -117.26) * mm});
            skLineSegment(sketch, "E9.30.7", {"start": v(4.69, -121.64) * mm, "end": v(5.07, -122.77) * mm});
            skLineSegment(sketch, "E9.30.8", {"start": v(-4.69, -121.64) * mm, "end": v(-5.07, -122.77) * mm});
            skArc(sketch, "E9.31.1", {"start": v(17.37, -120.49) * mm, "mid": v(16.61, -119.14) * mm, "end": v(15.66, -117.93) * mm});
            skArc(sketch, "E9.31.2", {"start": v(8.06, -121.47) * mm, "mid": v(8.52, -120) * mm, "end": v(9.2, -118.6) * mm});
            skArc(sketch, "E9.31.3", {"start": v(9.2, -118.6) * mm, "mid": v(10.49, -117.24) * mm, "end": v(12.26, -116.62) * mm});
            skArc(sketch, "E9.31.4", {"start": v(7.79, -122.62) * mm, "mid": v(7.32, -123.97) * mm, "end": v(6.56, -125.17) * mm});
            skArc(sketch, "E9.31.5", {"start": v(17.88, -121.56) * mm, "mid": v(18.62, -122.78) * mm, "end": v(19.6, -123.8) * mm});
            skArc(sketch, "E9.31.6", {"start": v(15.66, -117.93) * mm, "mid": v(14.12, -116.86) * mm, "end": v(12.26, -116.62) * mm});
            skLineSegment(sketch, "E9.31.7", {"start": v(17.37, -120.49) * mm, "end": v(17.88, -121.56) * mm});
            skLineSegment(sketch, "E9.31.8", {"start": v(8.06, -121.47) * mm, "end": v(7.79, -122.62) * mm});
            skArc(sketch, "E9.32.1", {"start": v(29.87, -118) * mm, "mid": v(28.98, -116.75) * mm, "end": v(27.9, -115.64) * mm});
            skArc(sketch, "E9.32.2", {"start": v(20.7, -119.96) * mm, "mid": v(21.02, -118.44) * mm, "end": v(21.55, -117) * mm});
            skArc(sketch, "E9.32.3", {"start": v(21.55, -117) * mm, "mid": v(22.69, -115.5) * mm, "end": v(24.38, -114.7) * mm});
            skArc(sketch, "E9.32.4", {"start": v(20.56, -121.14) * mm, "mid": v(20.24, -122.52) * mm, "end": v(19.6, -123.8) * mm});
            skArc(sketch, "E9.32.5", {"start": v(30.49, -119.03) * mm, "mid": v(31.35, -120.16) * mm, "end": v(32.44, -121.08) * mm});
            skArc(sketch, "E9.32.6", {"start": v(27.9, -115.64) * mm, "mid": v(26.25, -114.75) * mm, "end": v(24.38, -114.7) * mm});
            skLineSegment(sketch, "E9.32.7", {"start": v(29.87, -118) * mm, "end": v(30.49, -119.03) * mm});
            skLineSegment(sketch, "E9.32.8", {"start": v(20.7, -119.96) * mm, "end": v(20.56, -121.14) * mm});
            skArc(sketch, "E9.33.1", {"start": v(42.05, -114.24) * mm, "mid": v(41.02, -113.08) * mm, "end": v(39.84, -112.1) * mm});
            skArc(sketch, "E9.33.2", {"start": v(33.13, -117.14) * mm, "mid": v(33.28, -115.6) * mm, "end": v(33.66, -114.1) * mm});
            skArc(sketch, "E9.33.3", {"start": v(33.66, -114.1) * mm, "mid": v(34.64, -112.5) * mm, "end": v(36.24, -111.52) * mm});
            skArc(sketch, "E9.33.4", {"start": v(33.11, -118.33) * mm, "mid": v(32.93, -119.74) * mm, "end": v(32.44, -121.08) * mm});
            skArc(sketch, "E9.33.5", {"start": v(42.76, -115.2) * mm, "mid": v(43.74, -116.23) * mm, "end": v(44.92, -117.02) * mm});
            skArc(sketch, "E9.33.6", {"start": v(39.84, -112.1) * mm, "mid": v(38.1, -111.37) * mm, "end": v(36.24, -111.52) * mm});
            skLineSegment(sketch, "E9.33.7", {"start": v(42.05, -114.24) * mm, "end": v(42.76, -115.2) * mm});
            skLineSegment(sketch, "E9.33.8", {"start": v(33.13, -117.14) * mm, "end": v(33.11, -118.33) * mm});
            skArc(sketch, "E9.34.1", {"start": v(53.76, -109.22) * mm, "mid": v(52.62, -108.18) * mm, "end": v(51.34, -107.31) * mm});
            skArc(sketch, "E9.34.2", {"start": v(45.2, -113.03) * mm, "mid": v(45.18, -111.49) * mm, "end": v(45.4, -109.96) * mm});
            skArc(sketch, "E9.34.3", {"start": v(45.4, -109.96) * mm, "mid": v(46.2, -108.26) * mm, "end": v(47.7, -107.12) * mm});
            skArc(sketch, "E9.34.4", {"start": v(45.3, -114.22) * mm, "mid": v(45.27, -115.64) * mm, "end": v(44.92, -117.02) * mm});
            skArc(sketch, "E9.34.5", {"start": v(54.57, -110.1) * mm, "mid": v(55.65, -111.02) * mm, "end": v(56.9, -111.68) * mm});
            skArc(sketch, "E9.34.6", {"start": v(51.34, -107.31) * mm, "mid": v(49.54, -106.78) * mm, "end": v(47.7, -107.12) * mm});
            skLineSegment(sketch, "E9.34.7", {"start": v(53.76, -109.22) * mm, "end": v(54.57, -110.1) * mm});
            skLineSegment(sketch, "E9.34.8", {"start": v(45.2, -113.03) * mm, "end": v(45.3, -114.22) * mm});
            skArc(sketch, "E9.35.1", {"start": v(64.88, -103) * mm, "mid": v(63.64, -102.08) * mm, "end": v(62.27, -101.36) * mm});
            skArc(sketch, "E9.35.2", {"start": v(56.76, -107.69) * mm, "mid": v(56.59, -106.15) * mm, "end": v(56.64, -104.6) * mm});
            skArc(sketch, "E9.35.3", {"start": v(56.64, -104.6) * mm, "mid": v(57.27, -102.84) * mm, "end": v(58.63, -101.55) * mm});
            skArc(sketch, "E9.35.4", {"start": v(57, -108.85) * mm, "mid": v(57.1, -110.27) * mm, "end": v(56.9, -111.68) * mm});
            skArc(sketch, "E9.35.5", {"start": v(65.78, -103.78) * mm, "mid": v(66.95, -104.6) * mm, "end": v(68.27, -105.12) * mm});
            skArc(sketch, "E9.35.6", {"start": v(62.27, -101.36) * mm, "mid": v(60.43, -101.02) * mm, "end": v(58.63, -101.55) * mm});
            skLineSegment(sketch, "E9.35.7", {"start": v(64.88, -103) * mm, "end": v(65.78, -103.78) * mm});
            skLineSegment(sketch, "E9.35.8", {"start": v(56.76, -107.69) * mm, "end": v(57, -108.85) * mm});
            skArc(sketch, "E9.36.1", {"start": v(75.3, -95.66) * mm, "mid": v(73.96, -94.87) * mm, "end": v(72.53, -94.3) * mm});
            skArc(sketch, "E9.36.2", {"start": v(67.7, -101.16) * mm, "mid": v(67.38, -99.66) * mm, "end": v(67.27, -98.11) * mm});
            skArc(sketch, "E9.36.3", {"start": v(67.27, -98.11) * mm, "mid": v(67.7, -96.3) * mm, "end": v(68.92, -94.87) * mm});
            skArc(sketch, "E9.36.4", {"start": v(68.06, -102.3) * mm, "mid": v(68.32, -103.7) * mm, "end": v(68.27, -105.12) * mm});
            skArc(sketch, "E9.36.5", {"start": v(76.26, -96.34) * mm, "mid": v(77.51, -97.02) * mm, "end": v(78.88, -97.41) * mm});
            skArc(sketch, "E9.36.6", {"start": v(72.53, -94.3) * mm, "mid": v(70.66, -94.15) * mm, "end": v(68.92, -94.87) * mm});
            skLineSegment(sketch, "E9.36.7", {"start": v(75.3, -95.66) * mm, "end": v(76.26, -96.34) * mm});
            skLineSegment(sketch, "E9.36.8", {"start": v(67.7, -101.16) * mm, "end": v(68.06, -102.3) * mm});
            skArc(sketch, "E9.37.1", {"start": v(84.88, -87.26) * mm, "mid": v(83.47, -86.62) * mm, "end": v(81.98, -86.2) * mm});
            skArc(sketch, "E9.37.2", {"start": v(77.91, -93.53) * mm, "mid": v(77.42, -92.07) * mm, "end": v(77.16, -90.55) * mm});
            skArc(sketch, "E9.37.3", {"start": v(77.16, -90.55) * mm, "mid": v(77.4, -88.69) * mm, "end": v(78.46, -87.14) * mm});
            skArc(sketch, "E9.37.4", {"start": v(78.38, -94.63) * mm, "mid": v(78.79, -96) * mm, "end": v(78.88, -97.41) * mm});
            skArc(sketch, "E9.37.5", {"start": v(85.92, -87.84) * mm, "mid": v(87.23, -88.39) * mm, "end": v(88.63, -88.63) * mm});
            skArc(sketch, "E9.37.6", {"start": v(81.98, -86.2) * mm, "mid": v(80.11, -86.25) * mm, "end": v(78.46, -87.14) * mm});
            skLineSegment(sketch, "E9.37.7", {"start": v(84.88, -87.26) * mm, "end": v(85.92, -87.84) * mm});
            skLineSegment(sketch, "E9.37.8", {"start": v(77.91, -93.53) * mm, "end": v(78.38, -94.63) * mm});
            skArc(sketch, "E9.38.1", {"start": v(93.53, -77.91) * mm, "mid": v(92.07, -77.42) * mm, "end": v(90.55, -77.16) * mm});
            skArc(sketch, "E9.38.2", {"start": v(87.26, -84.88) * mm, "mid": v(86.62, -83.47) * mm, "end": v(86.2, -81.98) * mm});
            skArc(sketch, "E9.38.3", {"start": v(86.2, -81.98) * mm, "mid": v(86.25, -80.11) * mm, "end": v(87.14, -78.46) * mm});
            skArc(sketch, "E9.38.4", {"start": v(87.84, -85.92) * mm, "mid": v(88.39, -87.23) * mm, "end": v(88.63, -88.63) * mm});
            skArc(sketch, "E9.38.5", {"start": v(94.63, -78.38) * mm, "mid": v(96, -78.79) * mm, "end": v(97.41, -78.88) * mm});
            skArc(sketch, "E9.38.6", {"start": v(90.55, -77.16) * mm, "mid": v(88.69, -77.4) * mm, "end": v(87.14, -78.46) * mm});
            skLineSegment(sketch, "E9.38.7", {"start": v(93.53, -77.91) * mm, "end": v(94.63, -78.38) * mm});
            skLineSegment(sketch, "E9.38.8", {"start": v(87.26, -84.88) * mm, "end": v(87.84, -85.92) * mm});
            skArc(sketch, "E9.39.1", {"start": v(101.16, -67.7) * mm, "mid": v(99.66, -67.38) * mm, "end": v(98.11, -67.27) * mm});
            skArc(sketch, "E9.39.2", {"start": v(95.66, -75.3) * mm, "mid": v(94.87, -73.96) * mm, "end": v(94.3, -72.53) * mm});
            skArc(sketch, "E9.39.3", {"start": v(94.3, -72.53) * mm, "mid": v(94.15, -70.66) * mm, "end": v(94.87, -68.92) * mm});
            skArc(sketch, "E9.39.4", {"start": v(96.34, -76.26) * mm, "mid": v(97.02, -77.51) * mm, "end": v(97.41, -78.88) * mm});
            skArc(sketch, "E9.39.5", {"start": v(102.3, -68.06) * mm, "mid": v(103.7, -68.32) * mm, "end": v(105.12, -68.27) * mm});
            skArc(sketch, "E9.39.6", {"start": v(98.11, -67.27) * mm, "mid": v(96.3, -67.7) * mm, "end": v(94.87, -68.92) * mm});
            skLineSegment(sketch, "E9.39.7", {"start": v(101.16, -67.7) * mm, "end": v(102.3, -68.06) * mm});
            skLineSegment(sketch, "E9.39.8", {"start": v(95.66, -75.3) * mm, "end": v(96.34, -76.26) * mm});
            skArc(sketch, "E9.40.1", {"start": v(107.69, -56.76) * mm, "mid": v(106.15, -56.59) * mm, "end": v(104.6, -56.64) * mm});
            skArc(sketch, "E9.40.2", {"start": v(103, -64.88) * mm, "mid": v(102.08, -63.64) * mm, "end": v(101.36, -62.27) * mm});
            skArc(sketch, "E9.40.3", {"start": v(101.36, -62.27) * mm, "mid": v(101.02, -60.43) * mm, "end": v(101.55, -58.63) * mm});
            skArc(sketch, "E9.40.4", {"start": v(103.78, -65.78) * mm, "mid": v(104.6, -66.95) * mm, "end": v(105.12, -68.27) * mm});
            skArc(sketch, "E9.40.5", {"start": v(108.85, -57) * mm, "mid": v(110.27, -57.1) * mm, "end": v(111.68, -56.9) * mm});
            skArc(sketch, "E9.40.6", {"start": v(104.6, -56.64) * mm, "mid": v(102.84, -57.27) * mm, "end": v(101.55, -58.63) * mm});
            skLineSegment(sketch, "E9.40.7", {"start": v(107.69, -56.76) * mm, "end": v(108.85, -57) * mm});
            skLineSegment(sketch, "E9.40.8", {"start": v(103, -64.88) * mm, "end": v(103.78, -65.78) * mm});
            skArc(sketch, "E9.41.1", {"start": v(113.03, -45.2) * mm, "mid": v(111.49, -45.18) * mm, "end": v(109.96, -45.4) * mm});
            skArc(sketch, "E9.41.2", {"start": v(109.22, -53.76) * mm, "mid": v(108.18, -52.62) * mm, "end": v(107.31, -51.34) * mm});
            skArc(sketch, "E9.41.3", {"start": v(107.31, -51.34) * mm, "mid": v(106.78, -49.54) * mm, "end": v(107.12, -47.7) * mm});
            skArc(sketch, "E9.41.4", {"start": v(110.1, -54.57) * mm, "mid": v(111.02, -55.65) * mm, "end": v(111.68, -56.9) * mm});
            skArc(sketch, "E9.41.5", {"start": v(114.22, -45.3) * mm, "mid": v(115.64, -45.27) * mm, "end": v(117.02, -44.92) * mm});
            skArc(sketch, "E9.41.6", {"start": v(109.96, -45.4) * mm, "mid": v(108.26, -46.2) * mm, "end": v(107.12, -47.7) * mm});
            skLineSegment(sketch, "E9.41.7", {"start": v(113.03, -45.2) * mm, "end": v(114.22, -45.3) * mm});
            skLineSegment(sketch, "E9.41.8", {"start": v(109.22, -53.76) * mm, "end": v(110.1, -54.57) * mm});
            skArc(sketch, "E9.42.1", {"start": v(117.14, -33.13) * mm, "mid": v(115.6, -33.28) * mm, "end": v(114.1, -33.66) * mm});
            skArc(sketch, "E9.42.2", {"start": v(114.24, -42.05) * mm, "mid": v(113.08, -41.02) * mm, "end": v(112.1, -39.84) * mm});
            skArc(sketch, "E9.42.3", {"start": v(112.1, -39.84) * mm, "mid": v(111.37, -38.1) * mm, "end": v(111.52, -36.24) * mm});
            skArc(sketch, "E9.42.4", {"start": v(115.2, -42.76) * mm, "mid": v(116.23, -43.74) * mm, "end": v(117.02, -44.92) * mm});
            skArc(sketch, "E9.42.5", {"start": v(118.33, -33.11) * mm, "mid": v(119.74, -32.93) * mm, "end": v(121.08, -32.44) * mm});
            skArc(sketch, "E9.42.6", {"start": v(114.1, -33.66) * mm, "mid": v(112.5, -34.64) * mm, "end": v(111.52, -36.24) * mm});
            skLineSegment(sketch, "E9.42.7", {"start": v(117.14, -33.13) * mm, "end": v(118.33, -33.11) * mm});
            skLineSegment(sketch, "E9.42.8", {"start": v(114.24, -42.05) * mm, "end": v(115.2, -42.76) * mm});
            skArc(sketch, "E9.43.1", {"start": v(119.96, -20.7) * mm, "mid": v(118.44, -21.02) * mm, "end": v(117, -21.55) * mm});
            skArc(sketch, "E9.43.2", {"start": v(118, -29.87) * mm, "mid": v(116.75, -28.98) * mm, "end": v(115.64, -27.9) * mm});
            skArc(sketch, "E9.43.3", {"start": v(115.64, -27.9) * mm, "mid": v(114.75, -26.25) * mm, "end": v(114.7, -24.38) * mm});
            skArc(sketch, "E9.43.4", {"start": v(119.03, -30.49) * mm, "mid": v(120.16, -31.35) * mm, "end": v(121.08, -32.44) * mm});
            skArc(sketch, "E9.43.5", {"start": v(121.14, -20.56) * mm, "mid": v(122.52, -20.24) * mm, "end": v(123.8, -19.6) * mm});
            skArc(sketch, "E9.43.6", {"start": v(117, -21.55) * mm, "mid": v(115.5, -22.69) * mm, "end": v(114.7, -24.38) * mm});
            skLineSegment(sketch, "E9.43.7", {"start": v(119.96, -20.7) * mm, "end": v(121.14, -20.56) * mm});
            skLineSegment(sketch, "E9.43.8", {"start": v(118, -29.87) * mm, "end": v(119.03, -30.49) * mm});
            skArc(sketch, "E9.44.1", {"start": v(121.47, -8.06) * mm, "mid": v(120, -8.52) * mm, "end": v(118.6, -9.2) * mm});
            skArc(sketch, "E9.44.2", {"start": v(120.49, -17.37) * mm, "mid": v(119.14, -16.61) * mm, "end": v(117.93, -15.66) * mm});
            skArc(sketch, "E9.44.3", {"start": v(117.93, -15.66) * mm, "mid": v(116.86, -14.12) * mm, "end": v(116.62, -12.26) * mm});
            skArc(sketch, "E9.44.4", {"start": v(121.56, -17.88) * mm, "mid": v(122.78, -18.62) * mm, "end": v(123.8, -19.6) * mm});
            skArc(sketch, "E9.44.5", {"start": v(122.62, -7.79) * mm, "mid": v(123.97, -7.32) * mm, "end": v(125.17, -6.56) * mm});
            skArc(sketch, "E9.44.6", {"start": v(118.6, -9.2) * mm, "mid": v(117.24, -10.49) * mm, "end": v(116.62, -12.26) * mm});
            skLineSegment(sketch, "E9.44.7", {"start": v(121.47, -8.06) * mm, "end": v(122.62, -7.79) * mm});
            skLineSegment(sketch, "E9.44.8", {"start": v(120.49, -17.37) * mm, "end": v(121.56, -17.88) * mm});
            skArc(sketch, "E9.45.1", {"start": v(121.64, 4.69) * mm, "mid": v(120.23, 4.07) * mm, "end": v(118.92, 3.25) * mm});
            skArc(sketch, "E9.45.2", {"start": v(121.64, -4.69) * mm, "mid": v(120.23, -4.07) * mm, "end": v(118.92, -3.25) * mm});
            skArc(sketch, "E9.45.3", {"start": v(118.92, -3.25) * mm, "mid": v(117.7, -1.82) * mm, "end": v(117.26, 0) * mm});
            skArc(sketch, "E9.45.4", {"start": v(122.77, -5.07) * mm, "mid": v(124.05, -5.68) * mm, "end": v(125.17, -6.56) * mm});
            skArc(sketch, "E9.45.5", {"start": v(122.77, 5.07) * mm, "mid": v(124.05, 5.68) * mm, "end": v(125.17, 6.56) * mm});
            skArc(sketch, "E9.45.6", {"start": v(118.92, 3.25) * mm, "mid": v(117.7, 1.82) * mm, "end": v(117.26, 0) * mm});
            skLineSegment(sketch, "E9.45.7", {"start": v(121.64, 4.69) * mm, "end": v(122.77, 5.07) * mm});
            skLineSegment(sketch, "E9.45.8", {"start": v(121.64, -4.69) * mm, "end": v(122.77, -5.07) * mm});
            skArc(sketch, "E9.46.1", {"start": v(120.49, 17.37) * mm, "mid": v(119.14, 16.61) * mm, "end": v(117.93, 15.66) * mm});
            skArc(sketch, "E9.46.2", {"start": v(121.47, 8.06) * mm, "mid": v(120, 8.52) * mm, "end": v(118.6, 9.2) * mm});
            skArc(sketch, "E9.46.3", {"start": v(118.6, 9.2) * mm, "mid": v(117.24, 10.49) * mm, "end": v(116.62, 12.26) * mm});
            skArc(sketch, "E9.46.4", {"start": v(122.62, 7.79) * mm, "mid": v(123.97, 7.32) * mm, "end": v(125.17, 6.56) * mm});
            skArc(sketch, "E9.46.5", {"start": v(121.56, 17.88) * mm, "mid": v(122.78, 18.62) * mm, "end": v(123.8, 19.6) * mm});
            skArc(sketch, "E9.46.6", {"start": v(117.93, 15.66) * mm, "mid": v(116.86, 14.12) * mm, "end": v(116.62, 12.26) * mm});
            skLineSegment(sketch, "E9.46.7", {"start": v(120.49, 17.37) * mm, "end": v(121.56, 17.88) * mm});
            skLineSegment(sketch, "E9.46.8", {"start": v(121.47, 8.06) * mm, "end": v(122.62, 7.79) * mm});
            skArc(sketch, "E9.47.1", {"start": v(118, 29.87) * mm, "mid": v(116.75, 28.98) * mm, "end": v(115.64, 27.9) * mm});
            skArc(sketch, "E9.47.2", {"start": v(119.96, 20.7) * mm, "mid": v(118.44, 21.02) * mm, "end": v(117, 21.55) * mm});
            skArc(sketch, "E9.47.3", {"start": v(117, 21.55) * mm, "mid": v(115.5, 22.69) * mm, "end": v(114.7, 24.38) * mm});
            skArc(sketch, "E9.47.4", {"start": v(121.14, 20.56) * mm, "mid": v(122.52, 20.24) * mm, "end": v(123.8, 19.6) * mm});
            skArc(sketch, "E9.47.5", {"start": v(119.03, 30.49) * mm, "mid": v(120.16, 31.35) * mm, "end": v(121.08, 32.44) * mm});
            skArc(sketch, "E9.47.6", {"start": v(115.64, 27.9) * mm, "mid": v(114.75, 26.25) * mm, "end": v(114.7, 24.38) * mm});
            skLineSegment(sketch, "E9.47.7", {"start": v(118, 29.87) * mm, "end": v(119.03, 30.49) * mm});
            skLineSegment(sketch, "E9.47.8", {"start": v(119.96, 20.7) * mm, "end": v(121.14, 20.56) * mm});
            skArc(sketch, "E9.48.1", {"start": v(114.24, 42.05) * mm, "mid": v(113.08, 41.02) * mm, "end": v(112.1, 39.84) * mm});
            skArc(sketch, "E9.48.2", {"start": v(117.14, 33.13) * mm, "mid": v(115.6, 33.28) * mm, "end": v(114.1, 33.66) * mm});
            skArc(sketch, "E9.48.3", {"start": v(114.1, 33.66) * mm, "mid": v(112.5, 34.64) * mm, "end": v(111.52, 36.24) * mm});
            skArc(sketch, "E9.48.4", {"start": v(118.33, 33.11) * mm, "mid": v(119.74, 32.93) * mm, "end": v(121.08, 32.44) * mm});
            skArc(sketch, "E9.48.5", {"start": v(115.2, 42.76) * mm, "mid": v(116.23, 43.74) * mm, "end": v(117.02, 44.92) * mm});
            skArc(sketch, "E9.48.6", {"start": v(112.1, 39.84) * mm, "mid": v(111.37, 38.1) * mm, "end": v(111.52, 36.24) * mm});
            skLineSegment(sketch, "E9.48.7", {"start": v(114.24, 42.05) * mm, "end": v(115.2, 42.76) * mm});
            skLineSegment(sketch, "E9.48.8", {"start": v(117.14, 33.13) * mm, "end": v(118.33, 33.11) * mm});
            skArc(sketch, "E9.49.1", {"start": v(109.22, 53.76) * mm, "mid": v(108.18, 52.62) * mm, "end": v(107.31, 51.34) * mm});
            skArc(sketch, "E9.49.2", {"start": v(113.03, 45.2) * mm, "mid": v(111.49, 45.18) * mm, "end": v(109.96, 45.4) * mm});
            skArc(sketch, "E9.49.3", {"start": v(109.96, 45.4) * mm, "mid": v(108.26, 46.2) * mm, "end": v(107.12, 47.7) * mm});
            skArc(sketch, "E9.49.4", {"start": v(114.22, 45.3) * mm, "mid": v(115.64, 45.27) * mm, "end": v(117.02, 44.92) * mm});
            skArc(sketch, "E9.49.5", {"start": v(110.1, 54.57) * mm, "mid": v(111.02, 55.65) * mm, "end": v(111.68, 56.9) * mm});
            skArc(sketch, "E9.49.6", {"start": v(107.31, 51.34) * mm, "mid": v(106.78, 49.54) * mm, "end": v(107.12, 47.7) * mm});
            skLineSegment(sketch, "E9.49.7", {"start": v(109.22, 53.76) * mm, "end": v(110.1, 54.57) * mm});
            skLineSegment(sketch, "E9.49.8", {"start": v(113.03, 45.2) * mm, "end": v(114.22, 45.3) * mm});
            skArc(sketch, "E9.50.1", {"start": v(103, 64.88) * mm, "mid": v(102.08, 63.64) * mm, "end": v(101.36, 62.27) * mm});
            skArc(sketch, "E9.50.2", {"start": v(107.69, 56.76) * mm, "mid": v(106.15, 56.59) * mm, "end": v(104.6, 56.64) * mm});
            skArc(sketch, "E9.50.3", {"start": v(104.6, 56.64) * mm, "mid": v(102.84, 57.27) * mm, "end": v(101.55, 58.63) * mm});
            skArc(sketch, "E9.50.4", {"start": v(108.85, 57) * mm, "mid": v(110.27, 57.1) * mm, "end": v(111.68, 56.9) * mm});
            skArc(sketch, "E9.50.5", {"start": v(103.78, 65.78) * mm, "mid": v(104.6, 66.95) * mm, "end": v(105.12, 68.27) * mm});
            skArc(sketch, "E9.50.6", {"start": v(101.36, 62.27) * mm, "mid": v(101.02, 60.43) * mm, "end": v(101.55, 58.63) * mm});
            skLineSegment(sketch, "E9.50.7", {"start": v(103, 64.88) * mm, "end": v(103.78, 65.78) * mm});
            skLineSegment(sketch, "E9.50.8", {"start": v(107.69, 56.76) * mm, "end": v(108.85, 57) * mm});
            skArc(sketch, "E9.51.1", {"start": v(95.66, 75.3) * mm, "mid": v(94.87, 73.96) * mm, "end": v(94.3, 72.53) * mm});
            skArc(sketch, "E9.51.2", {"start": v(101.16, 67.7) * mm, "mid": v(99.66, 67.38) * mm, "end": v(98.11, 67.27) * mm});
            skArc(sketch, "E9.51.3", {"start": v(98.11, 67.27) * mm, "mid": v(96.3, 67.7) * mm, "end": v(94.87, 68.92) * mm});
            skArc(sketch, "E9.51.4", {"start": v(102.3, 68.06) * mm, "mid": v(103.7, 68.32) * mm, "end": v(105.12, 68.27) * mm});
            skArc(sketch, "E9.51.5", {"start": v(96.34, 76.26) * mm, "mid": v(97.02, 77.51) * mm, "end": v(97.41, 78.88) * mm});
            skArc(sketch, "E9.51.6", {"start": v(94.3, 72.53) * mm, "mid": v(94.15, 70.66) * mm, "end": v(94.87, 68.92) * mm});
            skLineSegment(sketch, "E9.51.7", {"start": v(95.66, 75.3) * mm, "end": v(96.34, 76.26) * mm});
            skLineSegment(sketch, "E9.51.8", {"start": v(101.16, 67.7) * mm, "end": v(102.3, 68.06) * mm});
            skArc(sketch, "E9.52.1", {"start": v(87.26, 84.88) * mm, "mid": v(86.62, 83.47) * mm, "end": v(86.2, 81.98) * mm});
            skArc(sketch, "E9.52.2", {"start": v(93.53, 77.91) * mm, "mid": v(92.07, 77.42) * mm, "end": v(90.55, 77.16) * mm});
            skArc(sketch, "E9.52.3", {"start": v(90.55, 77.16) * mm, "mid": v(88.69, 77.4) * mm, "end": v(87.14, 78.46) * mm});
            skArc(sketch, "E9.52.4", {"start": v(94.63, 78.38) * mm, "mid": v(96, 78.79) * mm, "end": v(97.41, 78.88) * mm});
            skArc(sketch, "E9.52.5", {"start": v(87.84, 85.92) * mm, "mid": v(88.39, 87.23) * mm, "end": v(88.63, 88.63) * mm});
            skArc(sketch, "E9.52.6", {"start": v(86.2, 81.98) * mm, "mid": v(86.25, 80.11) * mm, "end": v(87.14, 78.46) * mm});
            skLineSegment(sketch, "E9.52.7", {"start": v(87.26, 84.88) * mm, "end": v(87.84, 85.92) * mm});
            skLineSegment(sketch, "E9.52.8", {"start": v(93.53, 77.91) * mm, "end": v(94.63, 78.38) * mm});
            skArc(sketch, "E9.53.1", {"start": v(77.91, 93.53) * mm, "mid": v(77.42, 92.07) * mm, "end": v(77.16, 90.55) * mm});
            skArc(sketch, "E9.53.2", {"start": v(84.88, 87.26) * mm, "mid": v(83.47, 86.62) * mm, "end": v(81.98, 86.2) * mm});
            skArc(sketch, "E9.53.3", {"start": v(81.98, 86.2) * mm, "mid": v(80.11, 86.25) * mm, "end": v(78.46, 87.14) * mm});
            skArc(sketch, "E9.53.4", {"start": v(85.92, 87.84) * mm, "mid": v(87.23, 88.39) * mm, "end": v(88.63, 88.63) * mm});
            skArc(sketch, "E9.53.5", {"start": v(78.38, 94.63) * mm, "mid": v(78.79, 96) * mm, "end": v(78.88, 97.41) * mm});
            skArc(sketch, "E9.53.6", {"start": v(77.16, 90.55) * mm, "mid": v(77.4, 88.69) * mm, "end": v(78.46, 87.14) * mm});
            skLineSegment(sketch, "E9.53.7", {"start": v(77.91, 93.53) * mm, "end": v(78.38, 94.63) * mm});
            skLineSegment(sketch, "E9.53.8", {"start": v(84.88, 87.26) * mm, "end": v(85.92, 87.84) * mm});
            skArc(sketch, "E9.54.1", {"start": v(67.7, 101.16) * mm, "mid": v(67.38, 99.66) * mm, "end": v(67.27, 98.11) * mm});
            skArc(sketch, "E9.54.2", {"start": v(75.3, 95.66) * mm, "mid": v(73.96, 94.87) * mm, "end": v(72.53, 94.3) * mm});
            skArc(sketch, "E9.54.3", {"start": v(72.53, 94.3) * mm, "mid": v(70.66, 94.15) * mm, "end": v(68.92, 94.87) * mm});
            skArc(sketch, "E9.54.4", {"start": v(76.26, 96.34) * mm, "mid": v(77.51, 97.02) * mm, "end": v(78.88, 97.41) * mm});
            skArc(sketch, "E9.54.5", {"start": v(68.06, 102.3) * mm, "mid": v(68.32, 103.7) * mm, "end": v(68.27, 105.12) * mm});
            skArc(sketch, "E9.54.6", {"start": v(67.27, 98.11) * mm, "mid": v(67.7, 96.3) * mm, "end": v(68.92, 94.87) * mm});
            skLineSegment(sketch, "E9.54.7", {"start": v(67.7, 101.16) * mm, "end": v(68.06, 102.3) * mm});
            skLineSegment(sketch, "E9.54.8", {"start": v(75.3, 95.66) * mm, "end": v(76.26, 96.34) * mm});
            skArc(sketch, "E9.55.1", {"start": v(56.76, 107.69) * mm, "mid": v(56.59, 106.15) * mm, "end": v(56.64, 104.6) * mm});
            skArc(sketch, "E9.55.2", {"start": v(64.88, 103) * mm, "mid": v(63.64, 102.08) * mm, "end": v(62.27, 101.36) * mm});
            skArc(sketch, "E9.55.3", {"start": v(62.27, 101.36) * mm, "mid": v(60.43, 101.02) * mm, "end": v(58.63, 101.55) * mm});
            skArc(sketch, "E9.55.4", {"start": v(65.78, 103.78) * mm, "mid": v(66.95, 104.6) * mm, "end": v(68.27, 105.12) * mm});
            skArc(sketch, "E9.55.5", {"start": v(57, 108.85) * mm, "mid": v(57.1, 110.27) * mm, "end": v(56.9, 111.68) * mm});
            skArc(sketch, "E9.55.6", {"start": v(56.64, 104.6) * mm, "mid": v(57.27, 102.84) * mm, "end": v(58.63, 101.55) * mm});
            skLineSegment(sketch, "E9.55.7", {"start": v(56.76, 107.69) * mm, "end": v(57, 108.85) * mm});
            skLineSegment(sketch, "E9.55.8", {"start": v(64.88, 103) * mm, "end": v(65.78, 103.78) * mm});
            skArc(sketch, "E9.56.1", {"start": v(45.2, 113.03) * mm, "mid": v(45.18, 111.49) * mm, "end": v(45.4, 109.96) * mm});
            skArc(sketch, "E9.56.2", {"start": v(53.76, 109.22) * mm, "mid": v(52.62, 108.18) * mm, "end": v(51.34, 107.31) * mm});
            skArc(sketch, "E9.56.3", {"start": v(51.34, 107.31) * mm, "mid": v(49.54, 106.78) * mm, "end": v(47.7, 107.12) * mm});
            skArc(sketch, "E9.56.4", {"start": v(54.57, 110.1) * mm, "mid": v(55.65, 111.02) * mm, "end": v(56.9, 111.68) * mm});
            skArc(sketch, "E9.56.5", {"start": v(45.3, 114.22) * mm, "mid": v(45.27, 115.64) * mm, "end": v(44.92, 117.02) * mm});
            skArc(sketch, "E9.56.6", {"start": v(45.4, 109.96) * mm, "mid": v(46.2, 108.26) * mm, "end": v(47.7, 107.12) * mm});
            skLineSegment(sketch, "E9.56.7", {"start": v(45.2, 113.03) * mm, "end": v(45.3, 114.22) * mm});
            skLineSegment(sketch, "E9.56.8", {"start": v(53.76, 109.22) * mm, "end": v(54.57, 110.1) * mm});
            skArc(sketch, "E9.57.1", {"start": v(33.13, 117.14) * mm, "mid": v(33.28, 115.6) * mm, "end": v(33.66, 114.1) * mm});
            skArc(sketch, "E9.57.2", {"start": v(42.05, 114.24) * mm, "mid": v(41.02, 113.08) * mm, "end": v(39.84, 112.1) * mm});
            skArc(sketch, "E9.57.3", {"start": v(39.84, 112.1) * mm, "mid": v(38.1, 111.37) * mm, "end": v(36.24, 111.52) * mm});
            skArc(sketch, "E9.57.4", {"start": v(42.76, 115.2) * mm, "mid": v(43.74, 116.23) * mm, "end": v(44.92, 117.02) * mm});
            skArc(sketch, "E9.57.5", {"start": v(33.11, 118.33) * mm, "mid": v(32.93, 119.74) * mm, "end": v(32.44, 121.08) * mm});
            skArc(sketch, "E9.57.6", {"start": v(33.66, 114.1) * mm, "mid": v(34.64, 112.5) * mm, "end": v(36.24, 111.52) * mm});
            skLineSegment(sketch, "E9.57.7", {"start": v(33.13, 117.14) * mm, "end": v(33.11, 118.33) * mm});
            skLineSegment(sketch, "E9.57.8", {"start": v(42.05, 114.24) * mm, "end": v(42.76, 115.2) * mm});
            skArc(sketch, "E9.58.1", {"start": v(20.7, 119.96) * mm, "mid": v(21.02, 118.44) * mm, "end": v(21.55, 117) * mm});
            skArc(sketch, "E9.58.2", {"start": v(29.87, 118) * mm, "mid": v(28.98, 116.75) * mm, "end": v(27.9, 115.64) * mm});
            skArc(sketch, "E9.58.3", {"start": v(27.9, 115.64) * mm, "mid": v(26.25, 114.75) * mm, "end": v(24.38, 114.7) * mm});
            skArc(sketch, "E9.58.4", {"start": v(30.49, 119.03) * mm, "mid": v(31.35, 120.16) * mm, "end": v(32.44, 121.08) * mm});
            skArc(sketch, "E9.58.5", {"start": v(20.56, 121.14) * mm, "mid": v(20.24, 122.52) * mm, "end": v(19.6, 123.8) * mm});
            skArc(sketch, "E9.58.6", {"start": v(21.55, 117) * mm, "mid": v(22.69, 115.5) * mm, "end": v(24.38, 114.7) * mm});
            skLineSegment(sketch, "E9.58.7", {"start": v(20.7, 119.96) * mm, "end": v(20.56, 121.14) * mm});
            skLineSegment(sketch, "E9.58.8", {"start": v(29.87, 118) * mm, "end": v(30.49, 119.03) * mm});
            skArc(sketch, "E9.59.1", {"start": v(8.06, 121.47) * mm, "mid": v(8.52, 120) * mm, "end": v(9.2, 118.6) * mm});
            skArc(sketch, "E9.59.2", {"start": v(17.37, 120.49) * mm, "mid": v(16.61, 119.14) * mm, "end": v(15.66, 117.93) * mm});
            skArc(sketch, "E9.59.3", {"start": v(15.66, 117.93) * mm, "mid": v(14.12, 116.86) * mm, "end": v(12.26, 116.62) * mm});
            skArc(sketch, "E9.59.4", {"start": v(17.88, 121.56) * mm, "mid": v(18.62, 122.78) * mm, "end": v(19.6, 123.8) * mm});
            skArc(sketch, "E9.59.5", {"start": v(7.79, 122.62) * mm, "mid": v(7.32, 123.97) * mm, "end": v(6.56, 125.17) * mm});
            skArc(sketch, "E9.59.6", {"start": v(9.2, 118.6) * mm, "mid": v(10.49, 117.24) * mm, "end": v(12.26, 116.62) * mm});
            skLineSegment(sketch, "E9.59.7", {"start": v(8.06, 121.47) * mm, "end": v(7.79, 122.62) * mm});
            skLineSegment(sketch, "E9.59.8", {"start": v(17.37, 120.49) * mm, "end": v(17.88, 121.56) * mm});
            skCircle(sketch, "E10", {"center": v(0, 0) * mm, "radius": 123.73 * mm});
            skCircle(sketch, "E11", {"center": v(0, 0) * mm, "radius": 114.76 * mm});
            skCircle(sketch, "E12", {"center": v(0, 0) * mm, "radius": 65 * mm});
            skCircle(sketch, "E13", {"center": v(0, 72) * mm, "radius": 5.25 * mm});
            skCircle(sketch, "E14.1.0", {"center": v(-68.48, 22.25) * mm, "radius": 5.25 * mm});
            skCircle(sketch, "E14.2.0", {"center": v(-42.32, -58.25) * mm, "radius": 5.25 * mm});
            skCircle(sketch, "E14.3.0", {"center": v(42.32, -58.25) * mm, "radius": 5.25 * mm});
            skCircle(sketch, "E14.4.0", {"center": v(68.48, 22.25) * mm, "radius": 5.25 * mm});
            skSolve(sketch);
        }
        {
            var Q0;
            Q0=makeQuery(id+"F0.imprint","IMPRINT",FACE,{"disambiguationData":[TD([[makeQuery(id+"F0.imprint","IMPRINT",EDGE,{"derivedFrom":sQuery(id+"F0.wireOp",EDGE,"E11")}),1.0]])]});
            extrude(context, id + "F1", {"entities" : qUnion([Q0]), "endBound" : BoundingType.SYMMETRIC, "depth" : 4.5 * mm});
        }
        {
            var Q0;
            Q0=makeQuery(id+"F0.imprint","IMPRINT",FACE,{"disambiguationData":[TD([[makeQuery(id+"F0.imprint","IMPRINT",EDGE,{"derivedFrom":sQuery(id+"F0.wireOp",EDGE,"E1")}),-1.0]])]});
            extrude(context, id + "F2", {"entities" : qUnion([Q0]), "operationType" : NewBodyOperationType.ADD, "endBound" : BoundingType.SYMMETRIC, "depth" : 3.16 * mm});
        }
        {
            var Q0;
            Q0=makeQuery(id+"F1.opExtrude","CAP_FACE",FACE,{"disambiguationData":[OSD([sQuery(id+"F0.wireOp",EDGE,"E11"),sQuery(id+"F0.wireOp",EDGE,"E12"),sQuery(id+"F0.wireOp",EDGE,"E13"),sQuery(id+"F0.wireOp",EDGE,"E14.1.0"),sQuery(id+"F0.wireOp",EDGE,"E14.2.0"),sQuery(id+"F0.wireOp",EDGE,"E14.3.0"),sQuery(id+"F0.wireOp",EDGE,"E14.4.0")])],"isStart":false});
            var sketch = newSketch(context, id + "F3", { "sketchPlane" : qUnion([Q0])});
            skLineSegment(sketch, "E15", {"start": v(70.52, 10.83) * mm, "end": v(107.16, 16.45) * mm});
            skLineSegment(sketch, "E16", {"start": v(50.7, -50.21) * mm, "end": v(77.02, -76.3) * mm});
            skArc(sketch, "E17", {"start": v(77.02, -76.3) * mm, "mid": v(81.94, -70.98) * mm, "end": v(86.5, -65.35) * mm});
            skArc(sketch, "E18", {"start": v(50.7, -50.21) * mm, "mid": v(53.93, -46.72) * mm, "end": v(56.93, -43.01) * mm});
            skLineSegment(sketch, "E19", {"start": v(71.34, 1.33) * mm, "end": v(108.4, 2.02) * mm});
            skLineSegment(sketch, "E20", {"start": v(71.35, -0.54) * mm, "end": v(108.4, -0.82) * mm});
            skLineSegment(sketch, "E21", {"start": v(70.64, -10.04) * mm, "end": v(107.33, -15.26) * mm});
            skLineSegment(sketch, "E22", {"start": v(70.35, -11.89) * mm, "end": v(106.9, -18.06) * mm});
            skLineSegment(sketch, "E23", {"start": v(68.14, -21.16) * mm, "end": v(103.53, -32.15) * mm});
            skLineSegment(sketch, "E24", {"start": v(67.56, -22.94) * mm, "end": v(102.66, -34.85) * mm});
            skLineSegment(sketch, "E25", {"start": v(63.9, -31.74) * mm, "end": v(97.1, -48.22) * mm});
            skLineSegment(sketch, "E26", {"start": v(63.05, -33.4) * mm, "end": v(95.8, -50.75) * mm});
            skLineSegment(sketch, "E27", {"start": v(58.04, -41.5) * mm, "end": v(88.18, -63.06) * mm});
            skLineSegment(sketch, "E28", {"start": v(56.93, -43.01) * mm, "end": v(86.5, -65.35) * mm});
            skArc(sketch, "E29.trimOffspring", {"start": v(108.4, 2.02) * mm, "mid": v(108.01, 9.26) * mm, "end": v(107.16, 16.45) * mm});
            skArc(sketch, "E30.trimOffspring", {"start": v(107.33, -15.26) * mm, "mid": v(108.11, -8.06) * mm, "end": v(108.4, -0.82) * mm});
            skArc(sketch, "E31.trimOffspring", {"start": v(103.53, -32.15) * mm, "mid": v(105.45, -25.16) * mm, "end": v(106.9, -18.06) * mm});
            skArc(sketch, "E32.trimOffspring", {"start": v(97.1, -48.22) * mm, "mid": v(100.1, -41.63) * mm, "end": v(102.66, -34.85) * mm});
            skArc(sketch, "E33.trimOffspring", {"start": v(88.18, -63.06) * mm, "mid": v(92.2, -57.03) * mm, "end": v(95.8, -50.75) * mm});
            skArc(sketch, "E34.trimOffspring", {"start": v(58.04, -41.5) * mm, "mid": v(60.68, -37.54) * mm, "end": v(63.05, -33.4) * mm});
            skArc(sketch, "E35.trimOffspring", {"start": v(63.9, -31.74) * mm, "mid": v(65.88, -27.4) * mm, "end": v(67.56, -22.94) * mm});
            skArc(sketch, "E36.trimOffspring", {"start": v(68.14, -21.16) * mm, "mid": v(69.4, -16.56) * mm, "end": v(70.35, -11.89) * mm});
            skArc(sketch, "E37.trimOffspring", {"start": v(70.64, -10.04) * mm, "mid": v(71.15, -5.3) * mm, "end": v(71.35, -0.54) * mm});
            skArc(sketch, "E38.trimOffspring", {"start": v(71.34, 1.33) * mm, "mid": v(71.09, 6.1) * mm, "end": v(70.52, 10.83) * mm});
            skLineSegment(sketch, "E39.1.0", {"start": v(42.7, 57.17) * mm, "end": v(64.87, 86.86) * mm});
            skLineSegment(sketch, "E39.1.1", {"start": v(57.4, 42.37) * mm, "end": v(87.23, 64.38) * mm});
            skArc(sketch, "E39.1.2", {"start": v(41.18, 58.27) * mm, "mid": v(37.2, 60.89) * mm, "end": v(33.05, 63.24) * mm});
            skArc(sketch, "E39.1.3", {"start": v(20.78, 68.26) * mm, "mid": v(16.17, 69.5) * mm, "end": v(11.5, 70.42) * mm});
            skArc(sketch, "E39.1.4", {"start": v(31.38, 64.08) * mm, "mid": v(27.03, 66.03) * mm, "end": v(22.56, 67.69) * mm});
            skLineSegment(sketch, "E39.1.5", {"start": v(51.25, 49.64) * mm, "end": v(77.87, 75.43) * mm});
            skLineSegment(sketch, "E39.1.6", {"start": v(41.18, 58.27) * mm, "end": v(62.57, 88.53) * mm});
            skArc(sketch, "E39.1.7", {"start": v(62.57, 88.53) * mm, "mid": v(56.52, 92.51) * mm, "end": v(50.21, 96.08) * mm});
            skLineSegment(sketch, "E39.1.8", {"start": v(49.93, 50.97) * mm, "end": v(75.87, 77.44) * mm});
            skArc(sketch, "E39.1.9", {"start": v(75.87, 77.44) * mm, "mid": v(70.52, 82.34) * mm, "end": v(64.87, 86.86) * mm});
            skLineSegment(sketch, "E39.1.10", {"start": v(31.38, 64.08) * mm, "end": v(47.68, 97.36) * mm});
            skLineSegment(sketch, "E39.1.11", {"start": v(33.05, 63.24) * mm, "end": v(50.21, 96.08) * mm});
            skArc(sketch, "E39.1.12", {"start": v(57.4, 42.37) * mm, "mid": v(54.45, 46.1) * mm, "end": v(51.25, 49.64) * mm});
            skLineSegment(sketch, "E39.1.13", {"start": v(22.56, 67.69) * mm, "end": v(34.28, 102.85) * mm});
            skArc(sketch, "E39.1.14", {"start": v(49.93, 50.97) * mm, "mid": v(46.42, 54.19) * mm, "end": v(42.7, 57.17) * mm});
            skLineSegment(sketch, "E39.1.15", {"start": v(20.78, 68.26) * mm, "end": v(31.57, 103.71) * mm});
            skArc(sketch, "E39.1.16", {"start": v(87.23, 64.38) * mm, "mid": v(82.73, 70.06) * mm, "end": v(77.87, 75.43) * mm});
            skArc(sketch, "E39.1.17", {"start": v(63.42, 32.7) * mm, "mid": v(61.1, 36.85) * mm, "end": v(58.5, 40.85) * mm});
            skArc(sketch, "E39.1.18", {"start": v(96.36, 49.67) * mm, "mid": v(92.83, 56) * mm, "end": v(88.88, 62.07) * mm});
            skLineSegment(sketch, "E39.1.19", {"start": v(63.42, 32.7) * mm, "end": v(96.36, 49.67) * mm});
            skLineSegment(sketch, "E39.1.20", {"start": v(11.5, 70.42) * mm, "end": v(17.47, 107) * mm});
            skArc(sketch, "E39.1.21", {"start": v(47.68, 97.36) * mm, "mid": v(41.07, 100.33) * mm, "end": v(34.28, 102.85) * mm});
            skArc(sketch, "E39.1.22", {"start": v(31.57, 103.71) * mm, "mid": v(24.57, 105.59) * mm, "end": v(17.47, 107) * mm});
            skLineSegment(sketch, "E39.1.23", {"start": v(58.5, 40.85) * mm, "end": v(88.88, 62.07) * mm});
            skLineSegment(sketch, "E39.2.0", {"start": v(-41.18, 58.27) * mm, "end": v(-62.57, 88.53) * mm});
            skLineSegment(sketch, "E39.2.1", {"start": v(-22.56, 67.7) * mm, "end": v(-34.27, 102.85) * mm});
            skArc(sketch, "E39.2.2", {"start": v(-42.69, 57.17) * mm, "mid": v(-46.41, 54.2) * mm, "end": v(-49.93, 50.97) * mm});
            skArc(sketch, "E39.2.3", {"start": v(-58.5, 40.85) * mm, "mid": v(-61.1, 36.86) * mm, "end": v(-63.42, 32.7) * mm});
            skArc(sketch, "E39.2.4", {"start": v(-51.25, 49.65) * mm, "mid": v(-54.45, 46.11) * mm, "end": v(-57.4, 42.37) * mm});
            skLineSegment(sketch, "E39.2.5", {"start": v(-31.38, 64.08) * mm, "end": v(-47.67, 97.37) * mm});
            skLineSegment(sketch, "E39.2.6", {"start": v(-42.69, 57.17) * mm, "end": v(-64.86, 86.87) * mm});
            skArc(sketch, "E39.2.7", {"start": v(-64.86, 86.87) * mm, "mid": v(-70.52, 82.34) * mm, "end": v(-75.86, 77.45) * mm});
            skLineSegment(sketch, "E39.2.8", {"start": v(-33.04, 63.24) * mm, "end": v(-50.2, 96.08) * mm});
            skArc(sketch, "E39.2.9", {"start": v(-50.2, 96.08) * mm, "mid": v(-56.51, 92.52) * mm, "end": v(-62.57, 88.53) * mm});
            skLineSegment(sketch, "E39.2.10", {"start": v(-51.25, 49.65) * mm, "end": v(-77.86, 75.43) * mm});
            skLineSegment(sketch, "E39.2.11", {"start": v(-49.93, 50.97) * mm, "end": v(-75.86, 77.45) * mm});
            skArc(sketch, "E39.2.12", {"start": v(-22.56, 67.7) * mm, "mid": v(-27.03, 66.03) * mm, "end": v(-31.38, 64.08) * mm});
            skLineSegment(sketch, "E39.2.13", {"start": v(-57.4, 42.37) * mm, "end": v(-87.22, 64.38) * mm});
            skArc(sketch, "E39.2.14", {"start": v(-33.04, 63.24) * mm, "mid": v(-37.2, 60.89) * mm, "end": v(-41.18, 58.27) * mm});
            skLineSegment(sketch, "E39.2.15", {"start": v(-58.5, 40.85) * mm, "end": v(-88.88, 62.08) * mm});
            skArc(sketch, "E39.2.16", {"start": v(-34.27, 102.85) * mm, "mid": v(-41.06, 100.33) * mm, "end": v(-47.67, 97.37) * mm});
            skArc(sketch, "E39.2.17", {"start": v(-11.5, 70.42) * mm, "mid": v(-16.17, 69.5) * mm, "end": v(-20.78, 68.26) * mm});
            skArc(sketch, "E39.2.18", {"start": v(-17.47, 107) * mm, "mid": v(-24.57, 105.59) * mm, "end": v(-31.57, 103.71) * mm});
            skLineSegment(sketch, "E39.2.19", {"start": v(-11.5, 70.42) * mm, "end": v(-17.47, 107) * mm});
            skLineSegment(sketch, "E39.2.20", {"start": v(-63.42, 32.7) * mm, "end": v(-96.36, 49.67) * mm});
            skArc(sketch, "E39.2.21", {"start": v(-77.86, 75.43) * mm, "mid": v(-82.73, 70.06) * mm, "end": v(-87.22, 64.38) * mm});
            skArc(sketch, "E39.2.22", {"start": v(-88.88, 62.08) * mm, "mid": v(-92.83, 56) * mm, "end": v(-96.36, 49.67) * mm});
            skLineSegment(sketch, "E39.2.23", {"start": v(-20.78, 68.26) * mm, "end": v(-31.57, 103.71) * mm});
            skLineSegment(sketch, "E39.3.0", {"start": v(-68.14, -21.16) * mm, "end": v(-103.54, -32.15) * mm});
            skLineSegment(sketch, "E39.3.1", {"start": v(-71.35, -0.53) * mm, "end": v(-108.4, -0.81) * mm});
            skArc(sketch, "E39.3.2", {"start": v(-67.56, -22.93) * mm, "mid": v(-65.88, -27.4) * mm, "end": v(-63.9, -31.73) * mm});
            skArc(sketch, "E39.3.3", {"start": v(-56.93, -43) * mm, "mid": v(-53.93, -46.71) * mm, "end": v(-50.7, -50.21) * mm});
            skArc(sketch, "E39.3.4", {"start": v(-63.05, -33.4) * mm, "mid": v(-60.68, -37.53) * mm, "end": v(-58.04, -41.5) * mm});
            skLineSegment(sketch, "E39.3.5", {"start": v(-70.64, -10.04) * mm, "end": v(-107.33, -15.25) * mm});
            skLineSegment(sketch, "E39.3.6", {"start": v(-67.56, -22.93) * mm, "end": v(-102.66, -34.85) * mm});
            skArc(sketch, "E39.3.7", {"start": v(-102.66, -34.85) * mm, "mid": v(-100.1, -41.62) * mm, "end": v(-97.1, -48.22) * mm});
            skLineSegment(sketch, "E39.3.8", {"start": v(-70.35, -11.88) * mm, "end": v(-106.9, -18.06) * mm});
            skArc(sketch, "E39.3.9", {"start": v(-106.9, -18.06) * mm, "mid": v(-105.45, -25.16) * mm, "end": v(-103.54, -32.15) * mm});
            skLineSegment(sketch, "E39.3.10", {"start": v(-63.05, -33.4) * mm, "end": v(-95.8, -50.74) * mm});
            skLineSegment(sketch, "E39.3.11", {"start": v(-63.9, -31.73) * mm, "end": v(-97.1, -48.22) * mm});
            skArc(sketch, "E39.3.12", {"start": v(-71.35, -0.53) * mm, "mid": v(-71.15, -5.3) * mm, "end": v(-70.64, -10.04) * mm});
            skLineSegment(sketch, "E39.3.13", {"start": v(-58.04, -41.5) * mm, "end": v(-88.18, -63.06) * mm});
            skArc(sketch, "E39.3.14", {"start": v(-70.35, -11.88) * mm, "mid": v(-69.4, -16.56) * mm, "end": v(-68.14, -21.16) * mm});
            skLineSegment(sketch, "E39.3.15", {"start": v(-56.93, -43) * mm, "end": v(-86.5, -65.35) * mm});
            skArc(sketch, "E39.3.16", {"start": v(-108.4, -0.81) * mm, "mid": v(-108.11, -8.05) * mm, "end": v(-107.33, -15.25) * mm});
            skArc(sketch, "E39.3.17", {"start": v(-70.52, 10.83) * mm, "mid": v(-71.09, 6.1) * mm, "end": v(-71.34, 1.33) * mm});
            skArc(sketch, "E39.3.18", {"start": v(-107.16, 16.45) * mm, "mid": v(-108.01, 9.26) * mm, "end": v(-108.4, 2.03) * mm});
            skLineSegment(sketch, "E39.3.19", {"start": v(-70.52, 10.83) * mm, "end": v(-107.16, 16.45) * mm});
            skLineSegment(sketch, "E39.3.20", {"start": v(-50.7, -50.21) * mm, "end": v(-77.02, -76.3) * mm});
            skArc(sketch, "E39.3.21", {"start": v(-95.8, -50.74) * mm, "mid": v(-92.2, -57.03) * mm, "end": v(-88.18, -63.06) * mm});
            skArc(sketch, "E39.3.22", {"start": v(-86.5, -65.35) * mm, "mid": v(-81.94, -70.98) * mm, "end": v(-77.02, -76.3) * mm});
            skLineSegment(sketch, "E39.3.23", {"start": v(-71.34, 1.33) * mm, "end": v(-108.4, 2.03) * mm});
            skLineSegment(sketch, "E40", {"start": v(-74.76, -5.57) * mm, "end": v(-104.81, -7.8) * mm});
            skLineSegment(sketch, "E41", {"start": v(-74.3, 6.37) * mm, "end": v(-104.23, 8.94) * mm});
            skLineSegment(sketch, "E42.2.0", {"start": v(63.75, -39.44) * mm, "end": v(89.38, -55.3) * mm});
            skLineSegment(sketch, "E42.2.1", {"start": v(56.37, -48.83) * mm, "end": v(79.07, -68.5) * mm});
            skLineSegment(sketch, "E42.3.0", {"start": v(57.2, 48.44) * mm, "end": v(80.2, 67.92) * mm});
            skLineSegment(sketch, "E42.3.1", {"start": v(63.86, 38.52) * mm, "end": v(89.58, 54.04) * mm});
            skLineSegment(sketch, "E42.4.0", {"start": v(-28.4, 69.38) * mm, "end": v(-39.81, 97.27) * mm});
            skLineSegment(sketch, "E42.4.1", {"start": v(-16.9, 72.63) * mm, "end": v(-23.71, 101.9) * mm});
            skSolve(sketch);
        }
        {
            var Q0;
            Q0=makeQuery(id+"F3.imprint","IMPRINT",FACE,{"disambiguationData":[TD([[makeQuery(id+"F3.imprint","IMPRINT",EDGE,{"derivedFrom":sQuery(id+"F3.wireOp",EDGE,"E39.3.4")}),-1.0]])]});
            var Q1;
            Q1=makeQuery(id+"F3.imprint","IMPRINT",FACE,{"disambiguationData":[TD([[makeQuery(id+"F3.imprint","IMPRINT",EDGE,{"derivedFrom":sQuery(id+"F3.wireOp",EDGE,"E39.3.2")}),-1.0]])]});
            var Q2;
            Q2=makeQuery(id+"F3.imprint","IMPRINT",FACE,{"disambiguationData":[TD([[makeQuery(id+"F3.imprint","IMPRINT",EDGE,{"derivedFrom":sQuery(id+"F3.wireOp",EDGE,"E39.3.3")}),-1.0]])]});
            var Q3;
            Q3=makeQuery(id+"F3.imprint","IMPRINT",FACE,{"disambiguationData":[TD([[makeQuery(id+"F3.imprint","IMPRINT",EDGE,{"derivedFrom":sQuery(id+"F3.wireOp",EDGE,"E39.3.0")}),-1.0]])]});
            var Q4;
            Q4=makeQuery(id+"F3.imprint","IMPRINT",FACE,{"disambiguationData":[TD([[makeQuery(id+"F3.imprint","IMPRINT",EDGE,{"derivedFrom":sQuery(id+"F3.wireOp",EDGE,"E39.2.3")}),-1.0]])]});
            var Q5;
            Q5=makeQuery(id+"F3.imprint","IMPRINT",FACE,{"disambiguationData":[TD([[makeQuery(id+"F3.imprint","IMPRINT",EDGE,{"derivedFrom":sQuery(id+"F3.wireOp",EDGE,"E39.2.2")}),-1.0]])]});
            var Q6;
            Q6=makeQuery(id+"F3.imprint","IMPRINT",FACE,{"disambiguationData":[TD([[makeQuery(id+"F3.imprint","IMPRINT",EDGE,{"derivedFrom":sQuery(id+"F3.wireOp",EDGE,"E39.2.0")}),-1.0]])]});
            var Q7;
            Q7=makeQuery(id+"F3.imprint","IMPRINT",FACE,{"disambiguationData":[TD([[makeQuery(id+"F3.imprint","IMPRINT",EDGE,{"derivedFrom":sQuery(id+"F3.wireOp",EDGE,"E39.2.4")}),-1.0]])]});
            var Q8;
            Q8=makeQuery(id+"F3.imprint","IMPRINT",FACE,{"disambiguationData":[TD([[makeQuery(id+"F3.imprint","IMPRINT",EDGE,{"derivedFrom":sQuery(id+"F3.wireOp",EDGE,"E39.1.3")}),-1.0]])]});
            var Q9;
            Q9=makeQuery(id+"F3.imprint","IMPRINT",FACE,{"disambiguationData":[TD([[makeQuery(id+"F3.imprint","IMPRINT",EDGE,{"derivedFrom":sQuery(id+"F3.wireOp",EDGE,"E39.1.4")}),-1.0]])]});
            var Q10;
            Q10=makeQuery(id+"F3.imprint","IMPRINT",FACE,{"disambiguationData":[TD([[makeQuery(id+"F3.imprint","IMPRINT",EDGE,{"derivedFrom":sQuery(id+"F3.wireOp",EDGE,"E39.1.2")}),-1.0]])]});
            var Q11;
            Q11=makeQuery(id+"F3.imprint","IMPRINT",FACE,{"disambiguationData":[TD([[makeQuery(id+"F3.imprint","IMPRINT",EDGE,{"derivedFrom":sQuery(id+"F3.wireOp",EDGE,"E39.1.0")}),-1.0]])]});
            var Q12;
            Q12=makeQuery(id+"F3.imprint","IMPRINT",FACE,{"disambiguationData":[TD([[makeQuery(id+"F3.imprint","IMPRINT",EDGE,{"derivedFrom":sQuery(id+"F3.wireOp",EDGE,"E15")}),-1.0]])]});
            var Q13;
            Q13=makeQuery(id+"F3.imprint","IMPRINT",FACE,{"disambiguationData":[TD([[makeQuery(id+"F3.imprint","IMPRINT",EDGE,{"derivedFrom":sQuery(id+"F3.wireOp",EDGE,"E20")}),-1.0]])]});
            var Q14;
            Q14=makeQuery(id+"F3.imprint","IMPRINT",FACE,{"disambiguationData":[TD([[makeQuery(id+"F3.imprint","IMPRINT",EDGE,{"derivedFrom":sQuery(id+"F3.wireOp",EDGE,"E22")}),-1.0]])]});
            var Q15;
            Q15=makeQuery(id+"F3.imprint","IMPRINT",FACE,{"disambiguationData":[TD([[makeQuery(id+"F3.imprint","IMPRINT",EDGE,{"derivedFrom":sQuery(id+"F3.wireOp",EDGE,"E24")}),-1.0]])]});
            extrude(context, id + "F4", {"entities" : qUnion([Q0, Q1, Q2, Q3, Q4, Q5, Q6, Q7, Q8, Q9, Q10, Q11, Q12, Q13, Q14, Q15]), "operationType" : NewBodyOperationType.REMOVE, "oppositeDirection" : true, "depth" : 4.5 * mm});
        }
        {
            var Q0;
            Q0=makeQuery(id+"F3.imprint","IMPRINT",FACE,{"disambiguationData":[TD([[makeQuery(id+"F3.imprint","IMPRINT",EDGE,{"derivedFrom":sQuery(id+"F3.wireOp",EDGE,"E39.3.1")}),1.0]])]});
            var Q1;
            Q1=makeQuery(id+"F3.imprint","IMPRINT",FACE,{"disambiguationData":[TD([[makeQuery(id+"F3.imprint","IMPRINT",EDGE,{"derivedFrom":sQuery(id+"F3.wireOp",EDGE,"E39.3.17")}),-1.0]])]});
            var Q2;
            Q2=makeQuery(id+"F3.imprint","IMPRINT",FACE,{"disambiguationData":[TD([[makeQuery(id+"F3.imprint","IMPRINT",EDGE,{"derivedFrom":sQuery(id+"F3.wireOp",EDGE,"E39.2.1")}),1.0]])]});
            var Q3;
            Q3=makeQuery(id+"F3.imprint","IMPRINT",FACE,{"disambiguationData":[TD([[makeQuery(id+"F3.imprint","IMPRINT",EDGE,{"derivedFrom":sQuery(id+"F3.wireOp",EDGE,"E39.2.17")}),-1.0]])]});
            var Q4;
            Q4=makeQuery(id+"F3.imprint","IMPRINT",FACE,{"disambiguationData":[TD([[makeQuery(id+"F3.imprint","IMPRINT",EDGE,{"derivedFrom":sQuery(id+"F3.wireOp",EDGE,"E39.1.1")}),1.0]])]});
            var Q5;
            Q5=makeQuery(id+"F3.imprint","IMPRINT",FACE,{"disambiguationData":[TD([[makeQuery(id+"F3.imprint","IMPRINT",EDGE,{"derivedFrom":sQuery(id+"F3.wireOp",EDGE,"E39.1.17")}),-1.0]])]});
            var Q6;
            Q6=makeQuery(id+"F3.imprint","IMPRINT",FACE,{"disambiguationData":[TD([[makeQuery(id+"F3.imprint","IMPRINT",EDGE,{"derivedFrom":sQuery(id+"F3.wireOp",EDGE,"E26")}),-1.0]])]});
            var Q7;
            Q7=makeQuery(id+"F3.imprint","IMPRINT",FACE,{"disambiguationData":[TD([[makeQuery(id+"F3.imprint","IMPRINT",EDGE,{"derivedFrom":sQuery(id+"F3.wireOp",EDGE,"E16")}),1.0]])]});
            extrude(context, id + "F5", {"entities" : qUnion([Q0, Q1, Q2, Q3, Q4, Q5, Q6, Q7]), "operationType" : NewBodyOperationType.REMOVE, "oppositeDirection" : true, "depth" : 2 * mm});
        }
        {
            var Q0;
            Q0=makeQuery(id+"F5.boolean.opBoolean","COPY",EDGE,{"derivedFrom":makeQuery(id+"F5.opExtrude","SWEPT_EDGE",EDGE,{"disambiguationData":[OSD([sQuery(id+"F3.wireOp",EDGE,"E39.3.1"),sQuery(id+"F3.wireOp",EDGE,"E39.3.12")])]})});
            var Q1;
            Q1=makeQuery(id+"F4.boolean.opBoolean","COPY",EDGE,{"derivedFrom":makeQuery(id+"F4.opExtrude","SWEPT_EDGE",EDGE,{"disambiguationData":[OSD([sQuery(id+"F3.wireOp",EDGE,"E39.3.8"),sQuery(id+"F3.wireOp",EDGE,"E39.3.14")])]})});
            var Q2;
            Q2=makeQuery(id+"F4.boolean.opBoolean","COPY",EDGE,{"derivedFrom":makeQuery(id+"F4.opExtrude","SWEPT_EDGE",EDGE,{"disambiguationData":[OSD([sQuery(id+"F3.wireOp",EDGE,"E39.3.2"),sQuery(id+"F3.wireOp",EDGE,"E39.3.6")])]})});
            var Q3;
            Q3=makeQuery(id+"F4.boolean.opBoolean","COPY",EDGE,{"derivedFrom":makeQuery(id+"F4.opExtrude","SWEPT_EDGE",EDGE,{"disambiguationData":[OSD([sQuery(id+"F3.wireOp",EDGE,"E39.3.4"),sQuery(id+"F3.wireOp",EDGE,"E39.3.10")])]})});
            var Q4;
            Q4=makeQuery(id+"F4.boolean.opBoolean","COPY",EDGE,{"derivedFrom":makeQuery(id+"F4.opExtrude","SWEPT_EDGE",EDGE,{"disambiguationData":[OSD([sQuery(id+"F3.wireOp",EDGE,"E39.3.3"),sQuery(id+"F3.wireOp",EDGE,"E39.3.15")])]})});
            var Q5;
            Q5=makeQuery(id+"F5.boolean.opBoolean","COPY",EDGE,{"derivedFrom":makeQuery(id+"F5.opExtrude","SWEPT_EDGE",EDGE,{"disambiguationData":[OSD([sQuery(id+"F3.wireOp",EDGE,"E39.3.17"),sQuery(id+"F3.wireOp",EDGE,"E39.3.19")])]})});
            var Q6;
            Q6=makeQuery(id+"F5.boolean.opBoolean","COPY",EDGE,{"derivedFrom":makeQuery(id+"F5.opExtrude","SWEPT_EDGE",EDGE,{"disambiguationData":[OSD([sQuery(id+"F3.wireOp",EDGE,"E39.3.17"),sQuery(id+"F3.wireOp",EDGE,"E39.3.23")])]})});
            var Q7;
            Q7=makeQuery(id+"F5.boolean.opBoolean","COPY",EDGE,{"derivedFrom":makeQuery(id+"F5.opExtrude","SWEPT_EDGE",EDGE,{"disambiguationData":[OSD([sQuery(id+"F3.wireOp",EDGE,"E39.3.5"),sQuery(id+"F3.wireOp",EDGE,"E39.3.12")])]})});
            var Q8;
            Q8=makeQuery(id+"F4.boolean.opBoolean","COPY",EDGE,{"derivedFrom":makeQuery(id+"F4.opExtrude","SWEPT_EDGE",EDGE,{"disambiguationData":[OSD([sQuery(id+"F3.wireOp",EDGE,"E39.3.0"),sQuery(id+"F3.wireOp",EDGE,"E39.3.14")])]})});
            var Q9;
            Q9=makeQuery(id+"F4.boolean.opBoolean","COPY",EDGE,{"derivedFrom":makeQuery(id+"F4.opExtrude","SWEPT_EDGE",EDGE,{"disambiguationData":[OSD([sQuery(id+"F3.wireOp",EDGE,"E39.3.2"),sQuery(id+"F3.wireOp",EDGE,"E39.3.11")])]})});
            var Q10;
            Q10=makeQuery(id+"F4.boolean.opBoolean","COPY",EDGE,{"derivedFrom":makeQuery(id+"F4.opExtrude","SWEPT_EDGE",EDGE,{"disambiguationData":[OSD([sQuery(id+"F3.wireOp",EDGE,"E39.3.4"),sQuery(id+"F3.wireOp",EDGE,"E39.3.13")])]})});
            var Q11;
            Q11=makeQuery(id+"F4.boolean.opBoolean","COPY",EDGE,{"derivedFrom":makeQuery(id+"F4.opExtrude","SWEPT_EDGE",EDGE,{"disambiguationData":[OSD([sQuery(id+"F3.wireOp",EDGE,"E39.3.3"),sQuery(id+"F3.wireOp",EDGE,"E39.3.20")])]})});
            var Q12;
            Q12=makeQuery(id+"F5.boolean.opBoolean","COPY",EDGE,{"derivedFrom":makeQuery(id+"F5.opExtrude","SWEPT_EDGE",EDGE,{"disambiguationData":[OSD([sQuery(id+"F3.wireOp",EDGE,"E39.3.18"),sQuery(id+"F3.wireOp",EDGE,"E39.3.19")])]})});
            var Q13;
            Q13=makeQuery(id+"F5.boolean.opBoolean","COPY",EDGE,{"derivedFrom":makeQuery(id+"F5.opExtrude","SWEPT_EDGE",EDGE,{"disambiguationData":[OSD([sQuery(id+"F3.wireOp",EDGE,"E39.3.1"),sQuery(id+"F3.wireOp",EDGE,"E39.3.16")])]})});
            var Q14;
            Q14=makeQuery(id+"F4.boolean.opBoolean","COPY",EDGE,{"derivedFrom":makeQuery(id+"F4.opExtrude","SWEPT_EDGE",EDGE,{"disambiguationData":[OSD([sQuery(id+"F3.wireOp",EDGE,"E39.3.8"),sQuery(id+"F3.wireOp",EDGE,"E39.3.9")])]})});
            var Q15;
            Q15=makeQuery(id+"F4.boolean.opBoolean","COPY",EDGE,{"derivedFrom":makeQuery(id+"F4.opExtrude","SWEPT_EDGE",EDGE,{"disambiguationData":[OSD([sQuery(id+"F3.wireOp",EDGE,"E39.3.6"),sQuery(id+"F3.wireOp",EDGE,"E39.3.7")])]})});
            var Q16;
            Q16=makeQuery(id+"F4.boolean.opBoolean","COPY",EDGE,{"derivedFrom":makeQuery(id+"F4.opExtrude","SWEPT_EDGE",EDGE,{"disambiguationData":[OSD([sQuery(id+"F3.wireOp",EDGE,"E39.3.10"),sQuery(id+"F3.wireOp",EDGE,"E39.3.21")])]})});
            var Q17;
            Q17=makeQuery(id+"F4.boolean.opBoolean","COPY",EDGE,{"derivedFrom":makeQuery(id+"F4.opExtrude","SWEPT_EDGE",EDGE,{"disambiguationData":[OSD([sQuery(id+"F3.wireOp",EDGE,"E39.3.15"),sQuery(id+"F3.wireOp",EDGE,"E39.3.22")])]})});
            var Q18;
            Q18=makeQuery(id+"F4.boolean.opBoolean","COPY",EDGE,{"derivedFrom":makeQuery(id+"F4.opExtrude","SWEPT_EDGE",EDGE,{"disambiguationData":[OSD([sQuery(id+"F3.wireOp",EDGE,"E39.3.20"),sQuery(id+"F3.wireOp",EDGE,"E39.3.22")])]})});
            var Q19;
            Q19=makeQuery(id+"F4.boolean.opBoolean","COPY",EDGE,{"derivedFrom":makeQuery(id+"F4.opExtrude","SWEPT_EDGE",EDGE,{"disambiguationData":[OSD([sQuery(id+"F3.wireOp",EDGE,"E39.3.13"),sQuery(id+"F3.wireOp",EDGE,"E39.3.21")])]})});
            var Q20;
            Q20=makeQuery(id+"F4.boolean.opBoolean","COPY",EDGE,{"derivedFrom":makeQuery(id+"F4.opExtrude","SWEPT_EDGE",EDGE,{"disambiguationData":[OSD([sQuery(id+"F3.wireOp",EDGE,"E39.3.7"),sQuery(id+"F3.wireOp",EDGE,"E39.3.11")])]})});
            var Q21;
            Q21=makeQuery(id+"F4.boolean.opBoolean","COPY",EDGE,{"derivedFrom":makeQuery(id+"F4.opExtrude","SWEPT_EDGE",EDGE,{"disambiguationData":[OSD([sQuery(id+"F3.wireOp",EDGE,"E39.3.0"),sQuery(id+"F3.wireOp",EDGE,"E39.3.9")])]})});
            var Q22;
            Q22=makeQuery(id+"F5.boolean.opBoolean","COPY",EDGE,{"derivedFrom":makeQuery(id+"F5.opExtrude","SWEPT_EDGE",EDGE,{"disambiguationData":[OSD([sQuery(id+"F3.wireOp",EDGE,"E39.3.5"),sQuery(id+"F3.wireOp",EDGE,"E39.3.16")])]})});
            var Q23;
            Q23=makeQuery(id+"F5.boolean.opBoolean","COPY",EDGE,{"derivedFrom":makeQuery(id+"F5.opExtrude","SWEPT_EDGE",EDGE,{"disambiguationData":[OSD([sQuery(id+"F3.wireOp",EDGE,"E39.3.18"),sQuery(id+"F3.wireOp",EDGE,"E39.3.23")])]})});
            var Q24;
            Q24=makeQuery(id+"F4.boolean.opBoolean","COPY",EDGE,{"derivedFrom":makeQuery(id+"F4.opExtrude","SWEPT_EDGE",EDGE,{"disambiguationData":[OSD([sQuery(id+"F3.wireOp",EDGE,"E39.2.15"),sQuery(id+"F3.wireOp",EDGE,"E39.2.22")])]})});
            var Q25;
            Q25=makeQuery(id+"F4.boolean.opBoolean","COPY",EDGE,{"derivedFrom":makeQuery(id+"F4.opExtrude","SWEPT_EDGE",EDGE,{"disambiguationData":[OSD([sQuery(id+"F3.wireOp",EDGE,"E39.2.10"),sQuery(id+"F3.wireOp",EDGE,"E39.2.21")])]})});
            var Q26;
            Q26=makeQuery(id+"F4.boolean.opBoolean","COPY",EDGE,{"derivedFrom":makeQuery(id+"F4.opExtrude","SWEPT_EDGE",EDGE,{"disambiguationData":[OSD([sQuery(id+"F3.wireOp",EDGE,"E39.2.6"),sQuery(id+"F3.wireOp",EDGE,"E39.2.7")])]})});
            var Q27;
            Q27=makeQuery(id+"F4.boolean.opBoolean","COPY",EDGE,{"derivedFrom":makeQuery(id+"F4.opExtrude","SWEPT_EDGE",EDGE,{"disambiguationData":[OSD([sQuery(id+"F3.wireOp",EDGE,"E39.2.8"),sQuery(id+"F3.wireOp",EDGE,"E39.2.9")])]})});
            var Q28;
            Q28=makeQuery(id+"F5.boolean.opBoolean","COPY",EDGE,{"derivedFrom":makeQuery(id+"F5.opExtrude","SWEPT_EDGE",EDGE,{"disambiguationData":[OSD([sQuery(id+"F3.wireOp",EDGE,"E39.2.1"),sQuery(id+"F3.wireOp",EDGE,"E39.2.16")])]})});
            var Q29;
            Q29=makeQuery(id+"F5.boolean.opBoolean","COPY",EDGE,{"derivedFrom":makeQuery(id+"F5.opExtrude","SWEPT_EDGE",EDGE,{"disambiguationData":[OSD([sQuery(id+"F3.wireOp",EDGE,"E39.2.18"),sQuery(id+"F3.wireOp",EDGE,"E39.2.19")])]})});
            var Q30;
            Q30=makeQuery(id+"F5.boolean.opBoolean","COPY",EDGE,{"derivedFrom":makeQuery(id+"F5.opExtrude","SWEPT_EDGE",EDGE,{"disambiguationData":[OSD([sQuery(id+"F3.wireOp",EDGE,"E39.2.18"),sQuery(id+"F3.wireOp",EDGE,"E39.2.23")])]})});
            var Q31;
            Q31=makeQuery(id+"F5.boolean.opBoolean","COPY",EDGE,{"derivedFrom":makeQuery(id+"F5.opExtrude","SWEPT_EDGE",EDGE,{"disambiguationData":[OSD([sQuery(id+"F3.wireOp",EDGE,"E39.2.5"),sQuery(id+"F3.wireOp",EDGE,"E39.2.16")])]})});
            var Q32;
            Q32=makeQuery(id+"F4.boolean.opBoolean","COPY",EDGE,{"derivedFrom":makeQuery(id+"F4.opExtrude","SWEPT_EDGE",EDGE,{"disambiguationData":[OSD([sQuery(id+"F3.wireOp",EDGE,"E39.2.0"),sQuery(id+"F3.wireOp",EDGE,"E39.2.9")])]})});
            var Q33;
            Q33=makeQuery(id+"F4.boolean.opBoolean","COPY",EDGE,{"derivedFrom":makeQuery(id+"F4.opExtrude","SWEPT_EDGE",EDGE,{"disambiguationData":[OSD([sQuery(id+"F3.wireOp",EDGE,"E39.2.7"),sQuery(id+"F3.wireOp",EDGE,"E39.2.11")])]})});
            var Q34;
            Q34=makeQuery(id+"F4.boolean.opBoolean","COPY",EDGE,{"derivedFrom":makeQuery(id+"F4.opExtrude","SWEPT_EDGE",EDGE,{"disambiguationData":[OSD([sQuery(id+"F3.wireOp",EDGE,"E39.2.13"),sQuery(id+"F3.wireOp",EDGE,"E39.2.21")])]})});
            var Q35;
            Q35=makeQuery(id+"F4.boolean.opBoolean","COPY",EDGE,{"derivedFrom":makeQuery(id+"F4.opExtrude","SWEPT_EDGE",EDGE,{"disambiguationData":[OSD([sQuery(id+"F3.wireOp",EDGE,"E39.2.20"),sQuery(id+"F3.wireOp",EDGE,"E39.2.22")])]})});
            var Q36;
            Q36=makeQuery(id+"F5.boolean.opBoolean","COPY",EDGE,{"derivedFrom":makeQuery(id+"F5.opExtrude","SWEPT_EDGE",EDGE,{"disambiguationData":[OSD([sQuery(id+"F3.wireOp",EDGE,"E39.2.17"),sQuery(id+"F3.wireOp",EDGE,"E39.2.23")])]})});
            var Q37;
            Q37=makeQuery(id+"F5.boolean.opBoolean","COPY",EDGE,{"derivedFrom":makeQuery(id+"F5.opExtrude","SWEPT_EDGE",EDGE,{"disambiguationData":[OSD([sQuery(id+"F3.wireOp",EDGE,"E39.2.5"),sQuery(id+"F3.wireOp",EDGE,"E39.2.12")])]})});
            var Q38;
            Q38=makeQuery(id+"F4.boolean.opBoolean","COPY",EDGE,{"derivedFrom":makeQuery(id+"F4.opExtrude","SWEPT_EDGE",EDGE,{"disambiguationData":[OSD([sQuery(id+"F3.wireOp",EDGE,"E39.2.2"),sQuery(id+"F3.wireOp",EDGE,"E39.2.11")])]})});
            var Q39;
            Q39=makeQuery(id+"F4.boolean.opBoolean","COPY",EDGE,{"derivedFrom":makeQuery(id+"F4.opExtrude","SWEPT_EDGE",EDGE,{"disambiguationData":[OSD([sQuery(id+"F3.wireOp",EDGE,"E39.2.4"),sQuery(id+"F3.wireOp",EDGE,"E39.2.13")])]})});
            var Q40;
            Q40=makeQuery(id+"F4.boolean.opBoolean","COPY",EDGE,{"derivedFrom":makeQuery(id+"F4.opExtrude","SWEPT_EDGE",EDGE,{"disambiguationData":[OSD([sQuery(id+"F3.wireOp",EDGE,"E39.2.3"),sQuery(id+"F3.wireOp",EDGE,"E39.2.20")])]})});
            var Q41;
            Q41=makeQuery(id+"F5.boolean.opBoolean","COPY",EDGE,{"derivedFrom":makeQuery(id+"F5.opExtrude","SWEPT_EDGE",EDGE,{"disambiguationData":[OSD([sQuery(id+"F3.wireOp",EDGE,"E39.2.17"),sQuery(id+"F3.wireOp",EDGE,"E39.2.19")])]})});
            var Q42;
            Q42=makeQuery(id+"F5.boolean.opBoolean","COPY",EDGE,{"derivedFrom":makeQuery(id+"F5.opExtrude","SWEPT_EDGE",EDGE,{"disambiguationData":[OSD([sQuery(id+"F3.wireOp",EDGE,"E39.2.1"),sQuery(id+"F3.wireOp",EDGE,"E39.2.12")])]})});
            var Q43;
            Q43=makeQuery(id+"F4.boolean.opBoolean","COPY",EDGE,{"derivedFrom":makeQuery(id+"F4.opExtrude","SWEPT_EDGE",EDGE,{"disambiguationData":[OSD([sQuery(id+"F3.wireOp",EDGE,"E39.2.8"),sQuery(id+"F3.wireOp",EDGE,"E39.2.14")])]})});
            var Q44;
            Q44=makeQuery(id+"F4.boolean.opBoolean","COPY",EDGE,{"derivedFrom":makeQuery(id+"F4.opExtrude","SWEPT_EDGE",EDGE,{"disambiguationData":[OSD([sQuery(id+"F3.wireOp",EDGE,"E39.2.2"),sQuery(id+"F3.wireOp",EDGE,"E39.2.6")])]})});
            var Q45;
            Q45=makeQuery(id+"F4.boolean.opBoolean","COPY",EDGE,{"derivedFrom":makeQuery(id+"F4.opExtrude","SWEPT_EDGE",EDGE,{"disambiguationData":[OSD([sQuery(id+"F3.wireOp",EDGE,"E39.2.4"),sQuery(id+"F3.wireOp",EDGE,"E39.2.10")])]})});
            var Q46;
            Q46=makeQuery(id+"F4.boolean.opBoolean","COPY",EDGE,{"derivedFrom":makeQuery(id+"F4.opExtrude","SWEPT_EDGE",EDGE,{"disambiguationData":[OSD([sQuery(id+"F3.wireOp",EDGE,"E39.2.3"),sQuery(id+"F3.wireOp",EDGE,"E39.2.15")])]})});
            var Q47;
            Q47=makeQuery(id+"F4.boolean.opBoolean","COPY",EDGE,{"derivedFrom":makeQuery(id+"F4.opExtrude","SWEPT_EDGE",EDGE,{"disambiguationData":[OSD([sQuery(id+"F3.wireOp",EDGE,"E39.1.2"),sQuery(id+"F3.wireOp",EDGE,"E39.1.6")])]})});
            var Q48;
            Q48=makeQuery(id+"F4.boolean.opBoolean","COPY",EDGE,{"derivedFrom":makeQuery(id+"F4.opExtrude","SWEPT_EDGE",EDGE,{"disambiguationData":[OSD([sQuery(id+"F3.wireOp",EDGE,"E39.1.8"),sQuery(id+"F3.wireOp",EDGE,"E39.1.14")])]})});
            var Q49;
            Q49=makeQuery(id+"F4.boolean.opBoolean","COPY",EDGE,{"derivedFrom":makeQuery(id+"F4.opExtrude","SWEPT_EDGE",EDGE,{"disambiguationData":[OSD([sQuery(id+"F3.wireOp",EDGE,"E39.1.4"),sQuery(id+"F3.wireOp",EDGE,"E39.1.10")])]})});
            var Q50;
            Q50=makeQuery(id+"F4.boolean.opBoolean","COPY",EDGE,{"derivedFrom":makeQuery(id+"F4.opExtrude","SWEPT_EDGE",EDGE,{"disambiguationData":[OSD([sQuery(id+"F3.wireOp",EDGE,"E39.1.3"),sQuery(id+"F3.wireOp",EDGE,"E39.1.15")])]})});
            var Q51;
            Q51=makeQuery(id+"F5.boolean.opBoolean","COPY",EDGE,{"derivedFrom":makeQuery(id+"F5.opExtrude","SWEPT_EDGE",EDGE,{"disambiguationData":[OSD([sQuery(id+"F3.wireOp",EDGE,"E39.1.17"),sQuery(id+"F3.wireOp",EDGE,"E39.1.19")])]})});
            var Q52;
            Q52=makeQuery(id+"F5.boolean.opBoolean","COPY",EDGE,{"derivedFrom":makeQuery(id+"F5.opExtrude","SWEPT_EDGE",EDGE,{"disambiguationData":[OSD([sQuery(id+"F3.wireOp",EDGE,"E39.1.1"),sQuery(id+"F3.wireOp",EDGE,"E39.1.12")])]})});
            var Q53;
            Q53=makeQuery(id+"F4.boolean.opBoolean","COPY",EDGE,{"derivedFrom":makeQuery(id+"F4.opExtrude","SWEPT_EDGE",EDGE,{"disambiguationData":[OSD([sQuery(id+"F3.wireOp",EDGE,"E39.1.3"),sQuery(id+"F3.wireOp",EDGE,"E39.1.20")])]})});
            var Q54;
            Q54=makeQuery(id+"F4.boolean.opBoolean","COPY",EDGE,{"derivedFrom":makeQuery(id+"F4.opExtrude","SWEPT_EDGE",EDGE,{"disambiguationData":[OSD([sQuery(id+"F3.wireOp",EDGE,"E39.1.4"),sQuery(id+"F3.wireOp",EDGE,"E39.1.13")])]})});
            var Q55;
            Q55=makeQuery(id+"F4.boolean.opBoolean","COPY",EDGE,{"derivedFrom":makeQuery(id+"F4.opExtrude","SWEPT_EDGE",EDGE,{"disambiguationData":[OSD([sQuery(id+"F3.wireOp",EDGE,"E39.1.2"),sQuery(id+"F3.wireOp",EDGE,"E39.1.11")])]})});
            var Q56;
            Q56=makeQuery(id+"F4.boolean.opBoolean","COPY",EDGE,{"derivedFrom":makeQuery(id+"F4.opExtrude","SWEPT_EDGE",EDGE,{"disambiguationData":[OSD([sQuery(id+"F3.wireOp",EDGE,"E39.1.0"),sQuery(id+"F3.wireOp",EDGE,"E39.1.14")])]})});
            var Q57;
            Q57=makeQuery(id+"F5.boolean.opBoolean","COPY",EDGE,{"derivedFrom":makeQuery(id+"F5.opExtrude","SWEPT_EDGE",EDGE,{"disambiguationData":[OSD([sQuery(id+"F3.wireOp",EDGE,"E39.1.5"),sQuery(id+"F3.wireOp",EDGE,"E39.1.12")])]})});
            var Q58;
            Q58=makeQuery(id+"F5.boolean.opBoolean","COPY",EDGE,{"derivedFrom":makeQuery(id+"F5.opExtrude","SWEPT_EDGE",EDGE,{"disambiguationData":[OSD([sQuery(id+"F3.wireOp",EDGE,"E39.1.17"),sQuery(id+"F3.wireOp",EDGE,"E39.1.23")])]})});
            var Q59;
            Q59=makeQuery(id+"F5.boolean.opBoolean","COPY",EDGE,{"derivedFrom":makeQuery(id+"F5.opExtrude","SWEPT_EDGE",EDGE,{"disambiguationData":[OSD([sQuery(id+"F3.wireOp",EDGE,"E39.1.18"),sQuery(id+"F3.wireOp",EDGE,"E39.1.19")])]})});
            var Q60;
            Q60=makeQuery(id+"F5.boolean.opBoolean","COPY",EDGE,{"derivedFrom":makeQuery(id+"F5.opExtrude","SWEPT_EDGE",EDGE,{"disambiguationData":[OSD([sQuery(id+"F3.wireOp",EDGE,"E39.1.1"),sQuery(id+"F3.wireOp",EDGE,"E39.1.16")])]})});
            var Q61;
            Q61=makeQuery(id+"F4.boolean.opBoolean","COPY",EDGE,{"derivedFrom":makeQuery(id+"F4.opExtrude","SWEPT_EDGE",EDGE,{"disambiguationData":[OSD([sQuery(id+"F3.wireOp",EDGE,"E39.1.8"),sQuery(id+"F3.wireOp",EDGE,"E39.1.9")])]})});
            var Q62;
            Q62=makeQuery(id+"F4.boolean.opBoolean","COPY",EDGE,{"derivedFrom":makeQuery(id+"F4.opExtrude","SWEPT_EDGE",EDGE,{"disambiguationData":[OSD([sQuery(id+"F3.wireOp",EDGE,"E39.1.6"),sQuery(id+"F3.wireOp",EDGE,"E39.1.7")])]})});
            var Q63;
            Q63=makeQuery(id+"F4.boolean.opBoolean","COPY",EDGE,{"derivedFrom":makeQuery(id+"F4.opExtrude","SWEPT_EDGE",EDGE,{"disambiguationData":[OSD([sQuery(id+"F3.wireOp",EDGE,"E39.1.10"),sQuery(id+"F3.wireOp",EDGE,"E39.1.21")])]})});
            var Q64;
            Q64=makeQuery(id+"F4.boolean.opBoolean","COPY",EDGE,{"derivedFrom":makeQuery(id+"F4.opExtrude","SWEPT_EDGE",EDGE,{"disambiguationData":[OSD([sQuery(id+"F3.wireOp",EDGE,"E39.1.15"),sQuery(id+"F3.wireOp",EDGE,"E39.1.22")])]})});
            var Q65;
            Q65=makeQuery(id+"F5.boolean.opBoolean","COPY",EDGE,{"derivedFrom":makeQuery(id+"F5.opExtrude","SWEPT_EDGE",EDGE,{"disambiguationData":[OSD([sQuery(id+"F3.wireOp",EDGE,"E39.1.18"),sQuery(id+"F3.wireOp",EDGE,"E39.1.23")])]})});
            var Q66;
            Q66=makeQuery(id+"F5.boolean.opBoolean","COPY",EDGE,{"derivedFrom":makeQuery(id+"F5.opExtrude","SWEPT_EDGE",EDGE,{"disambiguationData":[OSD([sQuery(id+"F3.wireOp",EDGE,"E39.1.5"),sQuery(id+"F3.wireOp",EDGE,"E39.1.16")])]})});
            var Q67;
            Q67=makeQuery(id+"F4.boolean.opBoolean","COPY",EDGE,{"derivedFrom":makeQuery(id+"F4.opExtrude","SWEPT_EDGE",EDGE,{"disambiguationData":[OSD([sQuery(id+"F3.wireOp",EDGE,"E39.1.0"),sQuery(id+"F3.wireOp",EDGE,"E39.1.9")])]})});
            var Q68;
            Q68=makeQuery(id+"F4.boolean.opBoolean","COPY",EDGE,{"derivedFrom":makeQuery(id+"F4.opExtrude","SWEPT_EDGE",EDGE,{"disambiguationData":[OSD([sQuery(id+"F3.wireOp",EDGE,"E39.1.7"),sQuery(id+"F3.wireOp",EDGE,"E39.1.11")])]})});
            var Q69;
            Q69=makeQuery(id+"F4.boolean.opBoolean","COPY",EDGE,{"derivedFrom":makeQuery(id+"F4.opExtrude","SWEPT_EDGE",EDGE,{"disambiguationData":[OSD([sQuery(id+"F3.wireOp",EDGE,"E39.1.13"),sQuery(id+"F3.wireOp",EDGE,"E39.1.21")])]})});
            var Q70;
            Q70=makeQuery(id+"F4.boolean.opBoolean","COPY",EDGE,{"derivedFrom":makeQuery(id+"F4.opExtrude","SWEPT_EDGE",EDGE,{"disambiguationData":[OSD([sQuery(id+"F3.wireOp",EDGE,"E39.1.20"),sQuery(id+"F3.wireOp",EDGE,"E39.1.22")])]})});
            var Q71;
            Q71=makeQuery(id+"F4.boolean.opBoolean","COPY",EDGE,{"derivedFrom":makeQuery(id+"F4.opExtrude","SWEPT_EDGE",EDGE,{"disambiguationData":[OSD([sQuery(id+"F3.wireOp",EDGE,"E20"),sQuery(id+"F3.wireOp",EDGE,"E30.trimOffspring")])]})});
            var Q72;
            Q72=makeQuery(id+"F4.boolean.opBoolean","COPY",EDGE,{"derivedFrom":makeQuery(id+"F4.opExtrude","SWEPT_EDGE",EDGE,{"disambiguationData":[OSD([sQuery(id+"F3.wireOp",EDGE,"E15"),sQuery(id+"F3.wireOp",EDGE,"E29.trimOffspring")])]})});
            var Q73;
            Q73=makeQuery(id+"F4.boolean.opBoolean","COPY",EDGE,{"derivedFrom":makeQuery(id+"F4.opExtrude","SWEPT_EDGE",EDGE,{"disambiguationData":[OSD([sQuery(id+"F3.wireOp",EDGE,"E22"),sQuery(id+"F3.wireOp",EDGE,"E31.trimOffspring")])]})});
            var Q74;
            Q74=makeQuery(id+"F4.boolean.opBoolean","COPY",EDGE,{"derivedFrom":makeQuery(id+"F4.opExtrude","SWEPT_EDGE",EDGE,{"disambiguationData":[OSD([sQuery(id+"F3.wireOp",EDGE,"E24"),sQuery(id+"F3.wireOp",EDGE,"E32.trimOffspring")])]})});
            var Q75;
            Q75=makeQuery(id+"F5.boolean.opBoolean","COPY",EDGE,{"derivedFrom":makeQuery(id+"F5.opExtrude","SWEPT_EDGE",EDGE,{"disambiguationData":[OSD([sQuery(id+"F3.wireOp",EDGE,"E26"),sQuery(id+"F3.wireOp",EDGE,"E33.trimOffspring")])]})});
            var Q76;
            Q76=makeQuery(id+"F5.boolean.opBoolean","COPY",EDGE,{"derivedFrom":makeQuery(id+"F5.opExtrude","SWEPT_EDGE",EDGE,{"disambiguationData":[OSD([sQuery(id+"F3.wireOp",EDGE,"E17"),sQuery(id+"F3.wireOp",EDGE,"E28")])]})});
            var Q77;
            Q77=makeQuery(id+"F5.boolean.opBoolean","COPY",EDGE,{"derivedFrom":makeQuery(id+"F5.opExtrude","SWEPT_EDGE",EDGE,{"disambiguationData":[OSD([sQuery(id+"F3.wireOp",EDGE,"E16"),sQuery(id+"F3.wireOp",EDGE,"E17")])]})});
            var Q78;
            Q78=makeQuery(id+"F5.boolean.opBoolean","COPY",EDGE,{"derivedFrom":makeQuery(id+"F5.opExtrude","SWEPT_EDGE",EDGE,{"disambiguationData":[OSD([sQuery(id+"F3.wireOp",EDGE,"E27"),sQuery(id+"F3.wireOp",EDGE,"E33.trimOffspring")])]})});
            var Q79;
            Q79=makeQuery(id+"F4.boolean.opBoolean","COPY",EDGE,{"derivedFrom":makeQuery(id+"F4.opExtrude","SWEPT_EDGE",EDGE,{"disambiguationData":[OSD([sQuery(id+"F3.wireOp",EDGE,"E25"),sQuery(id+"F3.wireOp",EDGE,"E32.trimOffspring")])]})});
            var Q80;
            Q80=makeQuery(id+"F4.boolean.opBoolean","COPY",EDGE,{"derivedFrom":makeQuery(id+"F4.opExtrude","SWEPT_EDGE",EDGE,{"disambiguationData":[OSD([sQuery(id+"F3.wireOp",EDGE,"E23"),sQuery(id+"F3.wireOp",EDGE,"E31.trimOffspring")])]})});
            var Q81;
            Q81=makeQuery(id+"F4.boolean.opBoolean","COPY",EDGE,{"derivedFrom":makeQuery(id+"F4.opExtrude","SWEPT_EDGE",EDGE,{"disambiguationData":[OSD([sQuery(id+"F3.wireOp",EDGE,"E21"),sQuery(id+"F3.wireOp",EDGE,"E30.trimOffspring")])]})});
            var Q82;
            Q82=makeQuery(id+"F4.boolean.opBoolean","COPY",EDGE,{"derivedFrom":makeQuery(id+"F4.opExtrude","SWEPT_EDGE",EDGE,{"disambiguationData":[OSD([sQuery(id+"F3.wireOp",EDGE,"E19"),sQuery(id+"F3.wireOp",EDGE,"E29.trimOffspring")])]})});
            var Q83;
            Q83=makeQuery(id+"F4.boolean.opBoolean","COPY",EDGE,{"derivedFrom":makeQuery(id+"F4.opExtrude","SWEPT_EDGE",EDGE,{"disambiguationData":[OSD([sQuery(id+"F3.wireOp",EDGE,"E15"),sQuery(id+"F3.wireOp",EDGE,"E38.trimOffspring")])]})});
            var Q84;
            Q84=makeQuery(id+"F4.boolean.opBoolean","COPY",EDGE,{"derivedFrom":makeQuery(id+"F4.opExtrude","SWEPT_EDGE",EDGE,{"disambiguationData":[OSD([sQuery(id+"F3.wireOp",EDGE,"E20"),sQuery(id+"F3.wireOp",EDGE,"E37.trimOffspring")])]})});
            var Q85;
            Q85=makeQuery(id+"F4.boolean.opBoolean","COPY",EDGE,{"derivedFrom":makeQuery(id+"F4.opExtrude","SWEPT_EDGE",EDGE,{"disambiguationData":[OSD([sQuery(id+"F3.wireOp",EDGE,"E22"),sQuery(id+"F3.wireOp",EDGE,"E36.trimOffspring")])]})});
            var Q86;
            Q86=makeQuery(id+"F4.boolean.opBoolean","COPY",EDGE,{"derivedFrom":makeQuery(id+"F4.opExtrude","SWEPT_EDGE",EDGE,{"disambiguationData":[OSD([sQuery(id+"F3.wireOp",EDGE,"E24"),sQuery(id+"F3.wireOp",EDGE,"E35.trimOffspring")])]})});
            var Q87;
            Q87=makeQuery(id+"F5.boolean.opBoolean","COPY",EDGE,{"derivedFrom":makeQuery(id+"F5.opExtrude","SWEPT_EDGE",EDGE,{"disambiguationData":[OSD([sQuery(id+"F3.wireOp",EDGE,"E26"),sQuery(id+"F3.wireOp",EDGE,"E34.trimOffspring")])]})});
            var Q88;
            Q88=makeQuery(id+"F5.boolean.opBoolean","COPY",EDGE,{"derivedFrom":makeQuery(id+"F5.opExtrude","SWEPT_EDGE",EDGE,{"disambiguationData":[OSD([sQuery(id+"F3.wireOp",EDGE,"E18"),sQuery(id+"F3.wireOp",EDGE,"E28")])]})});
            var Q89;
            Q89=makeQuery(id+"F5.boolean.opBoolean","COPY",EDGE,{"derivedFrom":makeQuery(id+"F5.opExtrude","SWEPT_EDGE",EDGE,{"disambiguationData":[OSD([sQuery(id+"F3.wireOp",EDGE,"E16"),sQuery(id+"F3.wireOp",EDGE,"E18")])]})});
            var Q90;
            Q90=makeQuery(id+"F5.boolean.opBoolean","COPY",EDGE,{"derivedFrom":makeQuery(id+"F5.opExtrude","SWEPT_EDGE",EDGE,{"disambiguationData":[OSD([sQuery(id+"F3.wireOp",EDGE,"E27"),sQuery(id+"F3.wireOp",EDGE,"E34.trimOffspring")])]})});
            var Q91;
            Q91=makeQuery(id+"F4.boolean.opBoolean","COPY",EDGE,{"derivedFrom":makeQuery(id+"F4.opExtrude","SWEPT_EDGE",EDGE,{"disambiguationData":[OSD([sQuery(id+"F3.wireOp",EDGE,"E25"),sQuery(id+"F3.wireOp",EDGE,"E35.trimOffspring")])]})});
            var Q92;
            Q92=makeQuery(id+"F4.boolean.opBoolean","COPY",EDGE,{"derivedFrom":makeQuery(id+"F4.opExtrude","SWEPT_EDGE",EDGE,{"disambiguationData":[OSD([sQuery(id+"F3.wireOp",EDGE,"E21"),sQuery(id+"F3.wireOp",EDGE,"E37.trimOffspring")])]})});
            var Q93;
            Q93=makeQuery(id+"F4.boolean.opBoolean","COPY",EDGE,{"derivedFrom":makeQuery(id+"F4.opExtrude","SWEPT_EDGE",EDGE,{"disambiguationData":[OSD([sQuery(id+"F3.wireOp",EDGE,"E19"),sQuery(id+"F3.wireOp",EDGE,"E38.trimOffspring")])]})});
            var Q94;
            Q94=makeQuery(id+"F4.boolean.opBoolean","COPY",EDGE,{"derivedFrom":makeQuery(id+"F4.opExtrude","SWEPT_EDGE",EDGE,{"disambiguationData":[OSD([sQuery(id+"F3.wireOp",EDGE,"E23"),sQuery(id+"F3.wireOp",EDGE,"E36.trimOffspring")])]})});
            var Q95;
            Q95=makeQuery(id+"F4.boolean.opBoolean","COPY",EDGE,{"derivedFrom":makeQuery(id+"F4.opExtrude","SWEPT_EDGE",EDGE,{"disambiguationData":[OSD([sQuery(id+"F3.wireOp",EDGE,"E39.2.0"),sQuery(id+"F3.wireOp",EDGE,"E39.2.14")])]})});
            fillet(context, id + "F6", {"entities" : qUnion([Q0, Q1, Q2, Q3, Q4, Q5, Q6, Q7, Q8, Q9, Q10, Q11, Q12, Q13, Q14, Q15, Q16, Q17, Q18, Q19, Q20, Q21, Q22, Q23, Q24, Q25, Q26, Q27, Q28, Q29, Q30, Q31, Q32, Q33, Q34, Q35, Q36, Q37, Q38, Q39, Q40, Q41, Q42, Q43, Q44, Q45, Q46, Q47, Q48, Q49, Q50, Q51, Q52, Q53, Q54, Q55, Q56, Q57, Q58, Q59, Q60, Q61, Q62, Q63, Q64, Q65, Q66, Q67, Q68, Q69, Q70, Q71, Q72, Q73, Q74, Q75, Q76, Q77, Q78, Q79, Q80, Q81, Q82, Q83, Q84, Q85, Q86, Q87, Q88, Q89, Q90, Q91, Q92, Q93, Q94, Q95]), "radius" : 2 * mm, "tangentPropagation" : true, "allowEdgeOverflow" : false});
        }
        {
            var Q0;
            Q0=makeQuery(id+"F3.imprint","IMPRINT",FACE,{"disambiguationData":[TD([[makeQuery(id+"F3.imprint","IMPRINT",EDGE,{"derivedFrom":sQuery(id+"F3.wireOp",EDGE,"E39.3.1")}),1.0]])]});
            var Q1;
            Q1=sQuery(id+"F3.wireOp",EDGE,"E40");
            var Q2;
            Q2=sQuery(id+"F3.wireOp",EDGE,"E41");
            var Q3;
            Q3=sQuery(id+"F3.wireOp",EDGE,"E42.4.0");
            var Q4;
            Q4=sQuery(id+"F3.wireOp",EDGE,"E42.4.1");
            var Q5;
            Q5=sQuery(id+"F3.wireOp",EDGE,"E42.3.0");
            var Q6;
            Q6=sQuery(id+"F3.wireOp",EDGE,"E42.3.1");
            var Q7;
            Q7=sQuery(id+"F3.wireOp",EDGE,"E42.2.0");
            var Q8;
            Q8=sQuery(id+"F3.wireOp",EDGE,"E42.2.1");
            extrude(context, id + "F7", {"entities" : qUnion([Q0]), "bodyType" : ToolBodyType.SURFACE, "surfaceEntities" : qUnion([Q1, Q2, Q3, Q4, Q5, Q6, Q7, Q8]), "depth" : 25.4 * mm});
        }
    });
